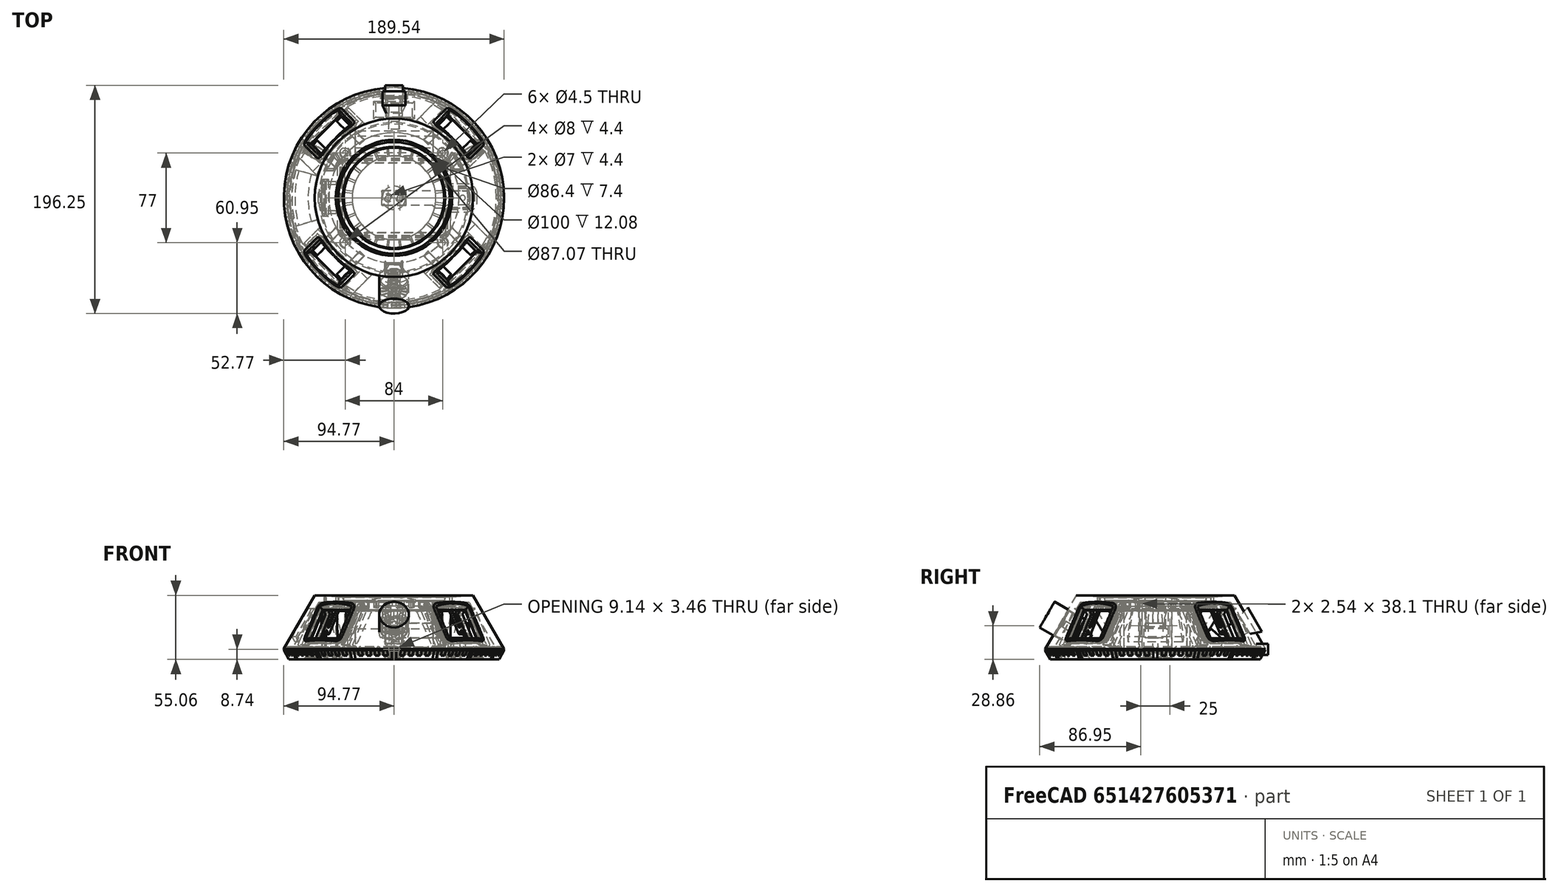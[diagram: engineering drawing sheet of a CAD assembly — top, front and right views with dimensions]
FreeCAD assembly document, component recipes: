
FREECAD ASSEMBLY — COMPONENT RECIPES ("case_v3_r2")

This assembly document has 20 components, labeled P0..P19 below (a component is one placed body or linked part). 20 of them carry a construction recipe — the FreeCAD feature program that regenerates the part from scratch, quoted from this document or its linked companion documents; the rest are supplied as boundary geometry only. No exploded tour is included for this assembly.
NOTE — document 2 of 2 of this assembly tour. The two overview renders and the header above are repeated from document 1; the component sections below continue where the previous document stopped.
COMPONENT P12 — recipe-attached ("link_loadcell", a linked part whose construction recipe lives in a companion FreeCAD document of the same project; that document's serialized recipe follows).
Construction recipe (the companion document, serialized — sketch geometry with constraints, then the solid features built on it; lengths are millimeters unless a unit is written):

FCSTD DOCUMENT  (FreeCAD 0.22R38340 (Git))
Label: parts_v3
License: All rights reserved
LicenseURL: https://en.wikipedia.org/wiki/All_rights_reserved
objects: PartDesign::Pad×24, Sketcher::SketchObject×20, Image::ImagePlane×7, PartDesign::Body×7, PartDesign::SubShapeBinder×2, PartDesign::Pocket×1
note: 124 computed .brp shape members not serialized (recipe doc carries the construction recipe); baked Part::Feature solids carry a one-line shape summary decoded from their .brp

FEATURE [Sketcher::SketchObject] Sketch001
  ArcFitTolerance = 1e-06
  AttachmentSupport = -> [XY_Plane001]
  FullyConstrained = false
  MakeInternals = false
  MapMode = 5
  sketch-geometry (26):
    g0: LineSegment StartX=-17.075 StartY=25.15 StartZ=0 EndX=-17.075 EndY=-31.25 EndZ=0
    g1: LineSegment StartX=-17.075 StartY=-31.25 StartZ=0 EndX=17.075 EndY=-31.25 EndZ=0
    g2: LineSegment StartX=17.075 StartY=-31.25 StartZ=0 EndX=17.075 EndY=25.149 EndZ=0
    g3: GeomPoint X=0 Y=0 Z=0
    g4: Circle CenterX=-15.125 CenterY=22.95 CenterZ=0 NormalX=0 NormalY=0 NormalZ=1 AngleXU=0 Radius=1
    g5: Circle CenterX=14.875 CenterY=22.95 CenterZ=0 NormalX=0 NormalY=0 NormalZ=1 AngleXU=0 Radius=1
    g6: Circle CenterX=14.875 CenterY=-29.05 CenterZ=0 NormalX=0 NormalY=0 NormalZ=1 AngleXU=0 Radius=1
    g7: Circle CenterX=-15.125 CenterY=-29.05 CenterZ=0 NormalX=0 NormalY=0 NormalZ=1 AngleXU=0 Radius=1
    g8: LineSegment StartX=-14.015 StartY=17.52 StartZ=0 EndX=-14.015 EndY=-17.52 EndZ=0
    g9: LineSegment StartX=-14.015 StartY=-17.52 StartZ=0 EndX=14.015 EndY=-17.52 EndZ=0
    g10: LineSegment StartX=14.015 StartY=-17.52 StartZ=0 EndX=14.015 EndY=17.52 EndZ=0
    g11: LineSegment StartX=14.015 StartY=17.52 StartZ=0 EndX=-14.015 EndY=17.52 EndZ=0
    g12: GeomPoint X=0 Y=0 Z=0
    g13: LineSegment StartX=-17.075 StartY=19.95 StartZ=0 EndX=-17.075 EndY=-23.9 EndZ=0
    g14: LineSegment StartX=-17.075 StartY=-23.9 StartZ=0 EndX=17.075 EndY=-23.9 EndZ=0
    g15: LineSegment StartX=17.075 StartY=-23.9 StartZ=0 EndX=17.075 EndY=19.95 EndZ=0
    g16: LineSegment StartX=17.075 StartY=19.95 StartZ=0 EndX=-17.075 EndY=19.95 EndZ=0
    g17: GeomPoint X=0 Y=-1.975 Z=0
    g18: LineSegment StartX=-11.575 StartY=25.149 StartZ=0 EndX=-11.575 EndY=20.95 EndZ=0
    g19: LineSegment StartX=-11.575 StartY=20.95 StartZ=0 EndX=11.575 EndY=20.95 EndZ=0
    g20: LineSegment StartX=11.575 StartY=20.95 StartZ=0 EndX=11.575 EndY=25.149 EndZ=0
    g21: LineSegment StartX=11.575 StartY=25.149 StartZ=0 EndX=-11.575 EndY=25.149 EndZ=0
    g22: LineSegment StartX=14.875 StartY=-29.05 StartZ=0 EndX=17.075 EndY=-29.05 EndZ=0
    g23: LineSegment StartX=-11.575 StartY=25.149 StartZ=0 EndX=11.575 EndY=25.149 EndZ=0
    g24: LineSegment StartX=-17.075 StartY=25.15 StartZ=0 EndX=-11.575 EndY=25.149 EndZ=0
    g25: LineSegment StartX=11.575 StartY=25.149 StartZ=0 EndX=17.075 EndY=25.149 EndZ=0
  constraints (67):
    c: Coincident(g0,g1)
    c: Coincident(g1,g2)
    c: Vertical(g0)
    c: Vertical(g2)
    c: Coincident(g3,g-1)
    c: DistanceY(g0,g0) = 56.4
    c: Equal(g5,g4)
    c: Equal(g4,g6)
    c: Equal(g6,g7)
    c: Diameter(g5) = 2
    c: Horizontal(g4,g5)
    c: Vertical(g5,g6)
    c: Vertical(g7,g4)
    c: DistanceX(g7,g6) = 30
    c: Coincident(g8,g9)
    c: Coincident(g9,g10)
    c: Coincident(g10,g11)
    c: Coincident(g11,g8)
    c: Vertical(g8)
    c: Vertical(g10)
    c: Horizontal(g9)
    c: Horizontal(g11)
    c: Symmetric(g10,g8,g12)
    c: Coincident(g12,g3)
    c: DistanceY(g8,g8) = 35.04
    c: DistanceX(g9,g9) = 28.03
    c: Coincident(g13,g14)
    c: Coincident(g14,g15)
    c: Coincident(g15,g16)
    c: Coincident(g16,g13)
    c: Vertical(g13)
    c: Vertical(g15)
    c: Horizontal(g14)
    c: Horizontal(g16)
    c: Symmetric(g15,g13,g17)
    c: PointOnObject(g17,g-2)
    c: DistanceY(g13,g13) = 43.85
    c: DistanceY(g7,g4) = 52
    c: DistanceY(g4,g0) = 2.2
    c: DistanceY(g13,g0) = 5.2
    c: Coincident(g18,g19)
    c: Coincident(g19,g20)
    c: Coincident(g20,g21)
    c: Coincident(g21,g18)
    c: Vertical(g18)
    c: Vertical(g20)
    c: Horizontal(g19)
    c: Symmetric(g20,g18,g-2)
    c: DistanceX(g20,g2) = 5.5
    c: DistanceY(g18,g0) = 0.001
    c: DistanceY(g19,g15) = -1
    c: DistanceY(g8,g13) = 2.43
    c: DistanceX(g16,g16) = 34.15
    c: DistanceX(g0,g2) = 34.15
    c: DistanceY(g1,g14) = 7.35
    c: Horizontal(g1)
    c: Coincident(g22,g6)
    c: PointOnObject(g22,g2)
    c: Horizontal(g22)
    c: DistanceX(g22,g22) = 2.2
    c: PointOnObject(g14,g2)
    c: Horizontal(g6,g7)
    c: Coincident(g23,g18)
    c: Coincident(g23,g20)
    c: Coincident(g25,g20)
    c: Coincident(g25,g2)
    c: Horizontal(g25)
FEATURE [Image::ImagePlane] lcd_front
  Placement = pos=(-11.6,7.22,10) rot=(0,0,1;0rad)
  XSize = 60.46
  YSize = 79.2117
FEATURE [Image::ImagePlane] lcd_side
  Placement = pos=(0,3.4,-17.75) rot=(0,1,0;1.5708rad)
  XSize = 52.9027
  YSize = 78.7888
FEATURE [PartDesign::SubShapeBinder] Binder
  BindCopyOnChange = 0
  BindMode = 0
  ClaimChildren = false
  Context = -> Body001 [Binder.]
  Fuse = false
  MakeFace = true
  OffsetFill = false
  OffsetIntersection = false
  OffsetJoinType = 0
  OffsetOpenResult = false
  PartialLoad = false
  Placement = pos=(0,0,3.85) rot=(0,0,1;0rad)
  Refine = true
  Relative = true
  Support = -> [Sketch001[Edge16,Edge15,Edge18,Edge17]]
  _Version = 2
  expr: .Placement.Base.z = Pad004.Length + 0.2 mm
FEATURE [Image::ImagePlane] charger  label="charger_img"
  XSize = 201.411
  YSize = 256.437
FEATURE [Sketcher::SketchObject] Sketch002
  ArcFitTolerance = 1e-06
  AttachmentSupport = -> [XY_Plane002]
  FullyConstrained = true
  MakeInternals = false
  MapMode = 5
  sketch-geometry (10):
    g0: LineSegment StartX=-6 StartY=0 StartZ=0 EndX=-6 EndY=-1.6 EndZ=0
    g1: LineSegment StartX=-6 StartY=-16 StartZ=0 EndX=6 EndY=-16 EndZ=0
    g2: LineSegment StartX=6 StartY=-16 StartZ=0 EndX=6 EndY=-3.2 EndZ=0
    g3: LineSegment StartX=6 StartY=0 StartZ=0 EndX=-6 EndY=0 EndZ=0
    g4: GeomPoint X=-6 Y=-2.4 Z=0
    g5: GeomPoint X=6 Y=-2.4 Z=0
    g6: ArcOfCircle CenterX=-6 CenterY=-2.4 CenterZ=0 NormalX=0 NormalY=0 NormalZ=1 AngleXU=0 Radius=0.8 StartAngle=4.71239 EndAngle=7.85398
    g7: ArcOfCircle CenterX=6 CenterY=-2.4 CenterZ=0 NormalX=0 NormalY=0 NormalZ=1 AngleXU=0 Radius=0.8 StartAngle=1.5708 EndAngle=4.71239
    g8: LineSegment StartX=6 StartY=-1.6 StartZ=0 EndX=6 EndY=0 EndZ=0
    g9: LineSegment StartX=-6 StartY=-3.2 StartZ=0 EndX=-6 EndY=-16 EndZ=0
  constraints (29):
    c: Coincident(g9,g1)
    c: Coincident(g1,g2)
    c: Coincident(g8,g3)
    c: Coincident(g3,g0)
    c: Vertical(g0)
    c: Vertical(g2)
    c: Horizontal(g1)
    c: Horizontal(g3)
    c: Distance(g0,g8) = 12
    c: Distance(g1,g3) = 16
    c: Symmetric(g0,g8,g-1)
    c: PointOnObject(g4,g0)
    c: PointOnObject(g5,g2)
    c: Horizontal(g5,g4)
    c: DistanceY(g4,g0) = 2.4
    c: Coincident(g6,g4)
    c: PointOnObject(g6,g9)
    c: Coincident(g7,g5)
    c: PointOnObject(g7,g8)
    c: Equal(g6,g7)
    c: Radius(g6) = 0.8
    c: Coincident(g2,g7)
    c: PointOnObject(g8,g7)
    c: Coincident(g0,g6)
    c: PointOnObject(g9,g6)
    c: Vertical(g0,g6)
    c: Vertical(g7,g2)
    c: Vertical(g9)
    c: Vertical(g8)
FEATURE [Sketcher::SketchObject] Sketch003
  ArcFitTolerance = 1e-06
  AttachmentOffset = pos=(0,0,-1.3) rot=(0,0,1;0rad)
  AttachmentSupport = -> [XZ_Plane002]
  FullyConstrained = true
  MakeInternals = false
  MapMode = 5
  Placement = pos=(0,1.3,-3e-16) rot=(1,0,0;1.5708rad)
  expr: Constraints[22] = 6.69 mm + 0.2 mm
  expr: Constraints[23] = 4.4 mm + 0.1 mm
  expr: Constraints[7] = 8.94 mm + 0.2 mm
  expr: Constraints[8] = 3.26 mm + 0.2 mm
  sketch-geometry (10):
    g0: LineSegment StartX=-3.445 StartY=1.04 StartZ=0 EndX=3.445 EndY=1.04 EndZ=0
    g1: LineSegment StartX=4.57 StartY=2.165 StartZ=0 EndX=4.57 EndY=3.375 EndZ=0
    g2: LineSegment StartX=3.445 StartY=4.5 StartZ=0 EndX=-3.445 EndY=4.5 EndZ=0
    g3: LineSegment StartX=-4.57 StartY=3.375 StartZ=0 EndX=-4.57 EndY=2.165 EndZ=0
    g4: GeomPoint X=4.57 Y=4.5 Z=0
    g5: GeomPoint X=0 Y=2.77 Z=0
    g6: ArcOfCircle CenterX=3.445 CenterY=3.375 CenterZ=0 NormalX=0 NormalY=0 NormalZ=1 AngleXU=0 Radius=1.125 StartAngle=0 EndAngle=1.5708
    g7: ArcOfCircle CenterX=3.445 CenterY=2.165 CenterZ=0 NormalX=0 NormalY=0 NormalZ=1 AngleXU=0 Radius=1.125 StartAngle=4.71239 EndAngle=6.28319
    g8: ArcOfCircle CenterX=-3.445 CenterY=2.165 CenterZ=0 NormalX=0 NormalY=0 NormalZ=1 AngleXU=0 Radius=1.125 StartAngle=3.14159 EndAngle=4.71239
    g9: ArcOfCircle CenterX=-3.445 CenterY=3.375 CenterZ=0 NormalX=0 NormalY=0 NormalZ=1 AngleXU=0 Radius=1.125 StartAngle=1.5708 EndAngle=3.14159
  constraints (24):
    c: Horizontal(g0)
    c: Horizontal(g2)
    c: Vertical(g1)
    c: Vertical(g3)
    c: Symmetric(g2,g0,g5)
    c: PointOnObject(g4,g1)
    c: PointOnObject(g4,g2)
    c: Distance(g1,g3) = 9.14
    c: Distance(g0,g2) = 3.46
    c: PointOnObject(g5,g-2)
    c: Equal(g3,g1)
    c: Equal(g0,g2)
    c: Vertical(g0,g2)
    c: DistanceY(g1,g1) = 1.21
    c: Tangent(g6,g2) = -1.5708
    c: Tangent(g6,g1) = -1.5708
    c: Tangent(g7,g1) = -1.5708
    c: Tangent(g7,g0) = -1.5708
    c: Tangent(g8,g0) = -1.5708
    c: Tangent(g8,g3) = -1.5708
    c: Tangent(g9,g3) = -1.5708
    c: Tangent(g9,g2) = -1.5708
    c: DistanceX(g2,g2) = 6.89
    c: DistanceY(g2) = 4.5
FEATURE [PartDesign::Pad] Pad007
  Direction = (0,-1,2e-16)
  Length = 10
  Length2 = 10
  Placement = pos=(0,0,0) rot=(1,0,0;1.5708rad)
  Profile = -> Sketch003
  ReferenceAxis = -> Sketch003 [N_Axis]
  Refine = true
  Suppressed = false
  Type = 0
FEATURE [PartDesign::SubShapeBinder] Binder001
  BindCopyOnChange = 0
  BindMode = 0
  ClaimChildren = false
  Context = -> Body002 [Binder001.]
  Fuse = false
  MakeFace = true
  Offset = 3
  OffsetFill = false
  OffsetIntersection = false
  OffsetJoinType = 0
  OffsetOpenResult = false
  PartialLoad = false
  Refine = true
  Relative = true
  Support = -> [Sketch003]
  _Version = 2
FEATURE [PartDesign::Pad] Pad008
  BaseFeature = -> Pad007
  Direction = (0,-1,2e-16)
  Length = 10
  Length2 = 10
  Placement = pos=(0,0,0) rot=(1,0,0;1.5708rad)
  Profile = -> Binder001
  Refine = true
  Reversed = true
  Suppressed = false
  Type = 0
FEATURE [Sketcher::SketchObject] Sketch005
  ArcFitTolerance = 1e-06
  AttachmentSupport = -> [XY_Plane004]
  FullyConstrained = false
  MakeInternals = false
  MapMode = 5
  sketch-geometry (5):
    g0: Circle CenterX=0 CenterY=0 CenterZ=0 NormalX=0 NormalY=0 NormalZ=1 AngleXU=0 Radius=9.25
    g1: ArcOfCircle CenterX=0 CenterY=0 CenterZ=0 NormalX=0 NormalY=0 NormalZ=1 AngleXU=0 Radius=9.25 StartAngle=0.74724 EndAngle=5.53526
    g2: LineSegment StartX=6.7855 StartY=6.28645 StartZ=0 EndX=11.637 EndY=1.04978 EndZ=0
    g3: ArcOfCircle CenterX=10.5 CenterY=-0.00362076 CenterZ=0 NormalX=0 NormalY=0 NormalZ=1 AngleXU=0 Radius=1.55 StartAngle=5.53526 EndAngle=7.03042
    g4: LineSegment StartX=11.6363 StartY=-1.05781 StartZ=0 EndX=6.78116 EndY=-6.29114 EndZ=0
  constraints (10):
    c: Diameter(g0) = 18.5
    c: Coincident(g0,g-1)
    c: Coincident(g1,g0)
    c: PointOnObject(g1,g0)
    c: Tangent(g2,g3) = 1.5708
    c: Coincident(g4,g1)
    c: Tangent(g4,g0)
    c: Tangent(g3,g4) = 1.5708
    c: Tangent(g1,g2) = 1.5708
    c: Radius(g3) = 1.55
FEATURE [Sketcher::SketchObject] Sketch006
  ArcFitTolerance = 1e-06
  AttachmentSupport = -> [XY_Plane005]
  FullyConstrained = true
  MakeInternals = false
  MapMode = 5
  sketch-geometry (8):
    g0: LineSegment StartX=-8.8 StartY=0 StartZ=0 EndX=-12.0492 EndY=10 EndZ=0
    g1: LineSegment StartX=-12.0492 StartY=10 StartZ=0 EndX=12.0492 EndY=10 EndZ=0
    g2: LineSegment StartX=12.0492 StartY=10 StartZ=0 EndX=8.8 EndY=0 EndZ=0
    g3: LineSegment StartX=8.8 StartY=0 StartZ=0 EndX=6.8 EndY=0 EndZ=0
    g4: LineSegment StartX=6.8 StartY=0 StartZ=0 EndX=6.8 EndY=-17 EndZ=0
    g5: LineSegment StartX=6.8 StartY=-17 StartZ=0 EndX=-6.8 EndY=-17 EndZ=0
    g6: LineSegment StartX=-6.8 StartY=-17 StartZ=0 EndX=-6.8 EndY=0 EndZ=0
    g7: LineSegment StartX=-6.8 StartY=0 StartZ=0 EndX=-8.8 EndY=0 EndZ=0
  constraints (22):
    c: PointOnObject(g0,g-1)
    c: Coincident(g0,g1)
    c: Coincident(g1,g2)
    c: PointOnObject(g2,g-1)
    c: Coincident(g2,g3)
    c: PointOnObject(g3,g-1)
    c: Coincident(g3,g4)
    c: Vertical(g4)
    c: Horizontal(g5)
    c: Coincident(g6,g7)
    c: Coincident(g7,g0)
    c: Vertical(g6)
    c: Symmetric(g1,g0,g-2)
    c: Symmetric(g6,g3,g-2)
    c: Equal(g3,g7)
    c: DistanceX(g7,g7) = 2
    c: DistanceX(g6,g3) = 13.6
    c: Angle(g2,g3) = 1.88496
    c: DistanceY(g1) = 10
    c: DistanceY(g5) = -17
    c: Coincident(g4,g5)
    c: Coincident(g5,g6)
FEATURE [Image::ImagePlane] switch  label="switch001"
  Placement = pos=(4.15,-14.6,0) rot=(0,0,1;0rad)
  XSize = 46.4854
  YSize = 52.5152
FEATURE [Image::ImagePlane] switch001  label="switch002"
  Placement = pos=(0,-14.7,16.1) rot=(0,1,0;1.5708rad)
  XSize = 46.585
  YSize = 52.6277
FEATURE [Sketcher::SketchObject] Sketch007
  ArcFitTolerance = 1e-06
  AttachmentSupport = -> [YZ_Plane005]
  ExternalGeometry = -> [Sketch006]
  FullyConstrained = false
  MakeInternals = false
  MapMode = 5
  Placement = pos=(0,0,0) rot=(0.57735,0.57735,0.57735;2.0944rad)
  sketch-geometry (12):
    g0: LineSegment StartX=9.98307 StartY=9.79369 StartZ=0 EndX=9.98307 EndY=-9.79369 EndZ=0
    g1: LineSegment StartX=9.98307 StartY=-9.79369 StartZ=0 EndX=0 EndY=-6.55 EndZ=0
    g2: LineSegment StartX=0 StartY=-6.55 StartZ=0 EndX=0 EndY=-4.55 EndZ=0
    g3: LineSegment StartX=0 StartY=-4.55 StartZ=0 EndX=-17 EndY=-4.55 EndZ=0
    g4: LineSegment StartX=-17 StartY=-4.55 StartZ=0 EndX=-17 EndY=4.55 EndZ=0
    g5: LineSegment StartX=-17 StartY=4.55 StartZ=0 EndX=0 EndY=4.55 EndZ=0
    g6: LineSegment StartX=0 StartY=4.55 StartZ=0 EndX=0 EndY=6.55 EndZ=0
    g7: LineSegment StartX=0 StartY=6.55 StartZ=0 EndX=9.98307 EndY=9.79369 EndZ=0
    g8: LineSegment StartX=-35.1614 StartY=30.2524 StartZ=0 EndX=-35.1614 EndY=-33.0132 EndZ=0
    g9: LineSegment StartX=-35.1614 StartY=-33.0132 StartZ=0 EndX=30.785 EndY=-33.0132 EndZ=0
    g10: LineSegment StartX=30.785 StartY=-33.0132 StartZ=0 EndX=30.785 EndY=30.2524 EndZ=0
    g11: LineSegment StartX=30.785 StartY=30.2524 StartZ=0 EndX=-35.1614 EndY=30.2524 EndZ=0
  constraints (29):
    c: Coincident(g0,g1)
    c: PointOnObject(g1,g-2)
    c: Coincident(g1,g2)
    c: PointOnObject(g2,g-2)
    c: Coincident(g2,g3)
    c: Horizontal(g3)
    c: Coincident(g3,g4)
    c: Vertical(g4)
    c: Coincident(g4,g5)
    c: PointOnObject(g5,g-2)
    c: Horizontal(g5)
    c: Coincident(g5,g6)
    c: PointOnObject(g6,g-2)
    c: Coincident(g6,g7)
    c: Coincident(g0,g7)
    c: Equal(g6,g2)
    c: Symmetric(g0,g0,g-1)
    c: Equal(g7,g1)
    c: DistanceY(g2,g5) = 9.1
    c: DistanceY(g2,g2) = 2
    c: Angle(g1,g2) = 1.88496
    c: Coincident(g8,g9)
    c: Coincident(g9,g10)
    c: Coincident(g10,g11)
    c: Coincident(g11,g8)
    c: Vertical(g8)
    c: Vertical(g10)
    c: Horizontal(g9)
    c: Horizontal(g11)
FEATURE [PartDesign::Pad] Pad015
  Direction = (0,0,1)
  Length = 40
  Length2 = 10
  Midplane = true
  Profile = -> Sketch006
  ReferenceAxis = -> Sketch006 [N_Axis]
  Refine = true
  Suppressed = false
  Type = 0
FEATURE [PartDesign::Pocket] Pocket
  BaseFeature = -> Pad015
  Direction = (-1,0,0)
  Length = 5
  Length2 = 5
  Midplane = true
  Profile = -> Sketch007
  ReferenceAxis = -> Sketch007 [N_Axis]
  Refine = true
  Suppressed = false
  Type = 1
FEATURE [PartDesign::Body] Body005  label="switch"
  AllowCompound = false
  Group = -> [Sketch006,Sketch007,Pad015,Pocket]
  Origin = -> Origin005
  Tip = -> Pocket
FEATURE [PartDesign::Pad] Pad021
  BaseFeature = -> Pad008
  Direction = (0,0,1)
  Length = 4.5
  Length2 = 10
  Placement = pos=(0,0,0) rot=(1,0,0;1.5708rad)
  Profile = -> Sketch002
  ReferenceAxis = -> Sketch002 [N_Axis]
  Refine = true
  Suppressed = false
  Type = 0
FEATURE [Sketcher::SketchObject] Sketch008
  ArcFitTolerance = 1e-06
  AttachmentOffset = pos=(0,0,2) rot=(0,0,1;0rad)
  AttachmentSupport = -> [XY_Plane002]
  FullyConstrained = true
  MakeInternals = false
  MapMode = 5
  Placement = pos=(0,0,2) rot=(0,0,1;0rad)
  sketch-geometry (4):
    g0: LineSegment StartX=-7 StartY=0 StartZ=0 EndX=-7 EndY=-16 EndZ=0
    g1: LineSegment StartX=-7 StartY=-16 StartZ=0 EndX=7 EndY=-16 EndZ=0
    g2: LineSegment StartX=7 StartY=-16 StartZ=0 EndX=7 EndY=0 EndZ=0
    g3: LineSegment StartX=7 StartY=0 StartZ=0 EndX=-7 EndY=0 EndZ=0
  constraints (11):
    c: Coincident(g0,g1)
    c: Coincident(g1,g2)
    c: Coincident(g2,g3)
    c: Coincident(g3,g0)
    c: Vertical(g0)
    c: Vertical(g2)
    c: Horizontal(g3)
    c: PointOnObject(g0,g-1)
    c: Symmetric(g1,g0,g-2)
    c: DistanceY(g1) = -16
    c: DistanceX(g1,g1) = 14
FEATURE [PartDesign::Pad] Pad022
  BaseFeature = -> Pad021
  Direction = (0,0,1)
  Length = 3
  Length2 = 10
  Placement = pos=(0,0,0) rot=(1,0,0;1.5708rad)
  Profile = -> Sketch008
  ReferenceAxis = -> Sketch008 [N_Axis]
  Refine = true
  Suppressed = false
  Type = 0
FEATURE [PartDesign::Body] Body002  label="charger"
  AllowCompound = false
  Group = -> [Sketch002,Sketch003,Pad007,Binder001,Pad008,Pad021,Sketch008,Pad022]
  Origin = -> Origin002
  Tip = -> Pad022
FEATURE [Sketcher::SketchObject] Sketch010
  ArcFitTolerance = 1e-06
  AttachmentSupport = -> [XY_Plane006]
  FullyConstrained = true
  MakeInternals = false
  MapMode = 5
  sketch-geometry (13):
    g0: Circle CenterX=-32 CenterY=0 CenterZ=0 NormalX=0 NormalY=0 NormalZ=1 AngleXU=0 Radius=2
    g1: Circle CenterX=-22 CenterY=0 CenterZ=0 NormalX=0 NormalY=0 NormalZ=1 AngleXU=0 Radius=2
    g2: Circle CenterX=22 CenterY=0 CenterZ=0 NormalX=0 NormalY=0 NormalZ=1 AngleXU=0 Radius=2
    g3: Circle CenterX=32 CenterY=0 CenterZ=0 NormalX=0 NormalY=0 NormalZ=1 AngleXU=0 Radius=2
    g4: LineSegment StartX=-37.5 StartY=6.35 StartZ=0 EndX=-37.5 EndY=-6.35 EndZ=0
    g5: LineSegment StartX=-37.5 StartY=-6.35 StartZ=0 EndX=37.5 EndY=-6.35 EndZ=0
    g6: LineSegment StartX=37.5 StartY=-6.35 StartZ=0 EndX=37.5 EndY=6.35 EndZ=0
    g7: GeomPoint X=0 Y=0 Z=0
    g8: LineSegment StartX=6.5 StartY=6.35 StartZ=0 EndX=8.8 EndY=8.65 EndZ=0
    g9: LineSegment StartX=8.8 StartY=8.65 StartZ=0 EndX=37.5 EndY=8.65 EndZ=0
    g10: LineSegment StartX=37.5 StartY=8.65 StartZ=0 EndX=37.5 EndY=6.35 EndZ=0
    g11: LineSegment StartX=6.5 StartY=6.35 StartZ=0 EndX=-37.5 EndY=6.35 EndZ=0
    g12: LineSegment StartX=37.5 StartY=8.65 StartZ=0 EndX=37.5 EndY=6.35 EndZ=0
  constraints (35):
    c: PointOnObject(g0,g-1)
    c: PointOnObject(g1,g-1)
    c: PointOnObject(g3,g-1)
    c: Equal(g3,g2)
    c: Equal(g2,g1)
    c: Equal(g1,g0)
    c: Coincident(g4,g5)
    c: Coincident(g5,g6)
    c: Coincident(g11,g4)
    c: Vertical(g4)
    c: Vertical(g6)
    c: Horizontal(g5)
    c: Symmetric(g6,g4,g7)
    c: Coincident(g7,g-1)
    c: DistanceX(g11,g6) = 75
    c: DistanceY(g6,g6) = 12.7
    c: DistanceX(g0,g1) = 10
    c: DistanceX(g2,g3) = 10
    c: Diameter(g1) = 4
    c: DistanceX(g1,g2) = 44
    c: Symmetric(g1,g2,g-2)
    c: PointOnObject(g8,g11)
    c: Coincident(g8,g9)
    c: Horizontal(g9)
    c: Coincident(g10,g6)
    c: Vertical(g10)
    c: PointOnObject(g11,g8)
    c: Coincident(g9,g10)
    c: DistanceY(g5,g8) = 15
    c: Angle(g8,g9) = 2.35619
    c: DistanceX(g8,g6) = 31
    c: Horizontal(g11)
    c: Horizontal(g8,g6)
    c: Coincident(g12,g9)
    c: Coincident(g12,g6)
FEATURE [PartDesign::Pad] Pad024
  Direction = (0,0,1)
  Length = 12.7
  Length2 = 10
  Profile = -> Sketch010 [Edge7,Edge6,Edge5,Edge11,Edge10,Edge9,Edge8]
  ReferenceAxis = -> Sketch010 [N_Axis]
  Refine = true
  Suppressed = false
  Type = 0
FEATURE [PartDesign::Pad] Pad025  label="Pad_LOAD_SCREWS"
  BaseFeature = -> Pad024
  Direction = (0,0,1)
  Length = 15
  Length2 = 10
  Profile = -> Sketch010 [Edge1,Edge2]
  ReferenceAxis = -> Sketch010 [N_Axis]
  Refine = true
  Reversed = true
  Suppressed = false
  Type = 0
FEATURE [PartDesign::Pad] Pad026  label="Pad_FIXED_SCREWS"
  BaseFeature = -> Pad025
  Direction = (0,0,1)
  Length = 25
  Length2 = 10
  Profile = -> Sketch010 [Edge3,Edge4]
  ReferenceAxis = -> Sketch010 [N_Axis]
  Refine = true
  Suppressed = false
  Type = 0
FEATURE [PartDesign::Body] Body006  label="loadcell_mit_silikon"
  AllowCompound = false
  Group = -> [Sketch010,Pad024,Pad025,Pad026]
  Origin = -> Origin006
  Tip = -> Pad026
FEATURE [Sketcher::SketchObject] Sketch011
  ArcFitTolerance = 1e-06
  AttachmentSupport = -> [XY_Plane001]
  FullyConstrained = false
  MakeInternals = false
  MapMode = 5
  sketch-geometry (4):
    g0: LineSegment StartX=-19.075 StartY=27.15 StartZ=0 EndX=-19.075 EndY=-33.25 EndZ=0
    g1: LineSegment StartX=-19.075 StartY=-33.25 StartZ=0 EndX=17.075 EndY=-33.25 EndZ=0
    g2: LineSegment StartX=17.075 StartY=-33.25 StartZ=0 EndX=17.075 EndY=27.15 EndZ=0
    g3: LineSegment StartX=17.075 StartY=27.15 StartZ=0 EndX=-19.075 EndY=27.15 EndZ=0
  constraints (8):
    c: Coincident(g0,g1)
    c: Coincident(g1,g2)
    c: Coincident(g2,g3)
    c: Coincident(g3,g0)
    c: Vertical(g0)
    c: Vertical(g2)
    c: Horizontal(g1)
    c: Horizontal(g3)
FEATURE [PartDesign::Pad] Pad027
  Direction = (0,0,1)
  Length = 1.2
  Length2 = 10
  Profile = -> Sketch011
  ReferenceAxis = -> Sketch011 [N_Axis]
  Refine = true
  Suppressed = false
  Type = 0
FEATURE [PartDesign::Pad] Pad004
  BaseFeature = -> Pad027
  Direction = (0,0,1)
  Length = 3.65
  Length2 = 10
  Profile = -> Sketch001 [Edge21,Edge20,Edge19,Edge22]
  ReferenceAxis = -> Sketch001 [N_Axis]
  Refine = true
  Suppressed = false
  Type = 0
FEATURE [PartDesign::Pad] Pad005
  BaseFeature = -> Pad004
  Direction = (0,0,1)
  Length = 10
  Length2 = 1
  Profile = -> Binder
  Refine = true
  Suppressed = false
  TaperAngle = 35
  Type = 4
FEATURE [PartDesign::Pad] Pad028
  BaseFeature = -> Pad005
  Direction = (0,0,1)
  Length = 3.5
  Length2 = 10
  Profile = -> Sketch001 [Edge1,Edge4,Edge3,Edge2]
  ReferenceAxis = -> Sketch001 [N_Axis]
  Refine = true
  Suppressed = false
  TaperAngle = -10
  Type = 4
FEATURE [PartDesign::Body] Body001  label="display"
  AllowCompound = false
  Group = -> [Sketch001,Sketch011,Pad027,Pad004,Binder,Pad005,Pad028]
  Origin = -> Origin001
  Tip = -> Pad028
FEATURE [Sketcher::SketchObject] Sketch012
  ArcFitTolerance = 1e-06
  AttachmentSupport = -> [XY_Plane007]
  FullyConstrained = true
  MakeInternals = false
  MapMode = 5
  sketch-geometry (4):
    g0: LineSegment StartX=-5.9 StartY=7.25 StartZ=0 EndX=-5.9 EndY=-7.25 EndZ=0
    g1: LineSegment StartX=-5.9 StartY=-7.25 StartZ=0 EndX=5.9 EndY=-7.25 EndZ=0
    g2: LineSegment StartX=5.9 StartY=-7.25 StartZ=0 EndX=5.9 EndY=7.25 EndZ=0
    g3: LineSegment StartX=5.9 StartY=7.25 StartZ=0 EndX=-5.9 EndY=7.25 EndZ=0
  constraints (11):
    c: Coincident(g0,g1)
    c: Coincident(g1,g2)
    c: Coincident(g2,g3)
    c: Coincident(g3,g0)
    c: Vertical(g0)
    c: Vertical(g2)
    c: Horizontal(g1)
    c: Horizontal(g3)
    c: DistanceX(g3,g3) = 11.8
    c: Symmetric(g0,g2,g-1)
    c: DistanceY(g2,g2) = 14.5
FEATURE [PartDesign::Pad] Pad009
  Direction = (0,0,1)
  Length = 6.5
  Length2 = 10
  Profile = -> Sketch012
  ReferenceAxis = -> Sketch012 [N_Axis]
  Refine = true
  Reversed = true
  Suppressed = false
  Type = 0
FEATURE [Sketcher::SketchObject] Sketch013
  ArcFitTolerance = 1e-06
  AttachmentSupport = -> [XY_Plane007]
  FullyConstrained = true
  MakeInternals = false
  MapMode = 5
  sketch-geometry (1):
    g0: Circle CenterX=0 CenterY=0 CenterZ=0 NormalX=0 NormalY=0 NormalZ=1 AngleXU=0 Radius=3.5
  constraints (2):
    c: Diameter(g0) = 7
    c: Coincident(g0,g-1)
FEATURE [PartDesign::Pad] Pad010
  BaseFeature = -> Pad009
  Direction = (0,0,1)
  Length = 5
  Length2 = 10
  Profile = -> Sketch013
  ReferenceAxis = -> Sketch013 [N_Axis]
  Refine = true
  Suppressed = false
  Type = 0
FEATURE [Sketcher::SketchObject] Sketch014
  ArcFitTolerance = 1e-06
  AttachmentSupport = -> [XY_Plane007]
  FullyConstrained = true
  MakeInternals = false
  MapMode = 5
  sketch-geometry (1):
    g0: Circle CenterX=0 CenterY=0 CenterZ=0 NormalX=0 NormalY=0 NormalZ=1 AngleXU=0 Radius=3
  constraints (2):
    c: Diameter(g0) = 6
    c: Coincident(g0,g-1)
FEATURE [PartDesign::Pad] Pad011
  BaseFeature = -> Pad010
  Direction = (0,0,1)
  Length = 15
  Length2 = 10
  Profile = -> Sketch014
  ReferenceAxis = -> Sketch014 [N_Axis]
  Refine = true
  Suppressed = false
  Type = 0
FEATURE [Sketcher::SketchObject] Sketch015
  ArcFitTolerance = 1e-06
  AttachmentSupport = -> [XY_Plane007]
  FullyConstrained = false
  MakeInternals = false
  MapMode = 5
  sketch-geometry (8):
    g0: LineSegment StartX=-4.4052 StartY=7.5 StartZ=0 EndX=-4.4052 EndY=6.5 EndZ=0
    g1: LineSegment StartX=-4.4052 StartY=6.5 StartZ=0 EndX=4.47502 EndY=6.5 EndZ=0
    g2: LineSegment StartX=4.47502 StartY=6.5 StartZ=0 EndX=4.47502 EndY=7.5 EndZ=0
    g3: LineSegment StartX=4.47502 StartY=7.5 StartZ=0 EndX=-4.4052 EndY=7.5 EndZ=0
    g4: LineSegment StartX=-4.24166 StartY=-7 StartZ=0 EndX=-4.24166 EndY=-8 EndZ=0
    g5: LineSegment StartX=-4.24166 StartY=-8 StartZ=0 EndX=5.13629 EndY=-8 EndZ=0
    g6: LineSegment StartX=5.13629 StartY=-8 StartZ=0 EndX=5.13629 EndY=-7 EndZ=0
    g7: LineSegment StartX=5.13629 StartY=-7 StartZ=0 EndX=-4.24166 EndY=-7 EndZ=0
  constraints (20):
    c: Coincident(g0,g1)
    c: Coincident(g1,g2)
    c: Coincident(g2,g3)
    c: Coincident(g3,g0)
    c: Vertical(g0)
    c: Vertical(g2)
    c: Horizontal(g1)
    c: Horizontal(g3)
    c: Coincident(g4,g5)
    c: Coincident(g5,g6)
    c: Coincident(g6,g7)
    c: Coincident(g7,g4)
    c: Vertical(g4)
    c: Vertical(g6)
    c: Horizontal(g5)
    c: Horizontal(g7)
    c: DistanceY(g4) = -7
    c: DistanceY(g4,g4) = 1
    c: DistanceY(g0) = 6.5
    c: DistanceY(g0,g0) = 1
FEATURE [PartDesign::Pad] Pad012
  BaseFeature = -> Pad011
  Direction = (0,0,1)
  Length = 10
  Length2 = 10
  Profile = -> Sketch015
  ReferenceAxis = -> Sketch015 [N_Axis]
  Refine = true
  Reversed = true
  Suppressed = false
  Type = 0
FEATURE [PartDesign::Body] Body007  label="Encoder"
  AllowCompound = false
  Group = -> [Sketch012,Pad009,Sketch013,Pad010,Sketch014,Pad011,Sketch015,Pad012]
  Origin = -> Origin007
  Tip = -> Pad012
FEATURE [Sketcher::SketchObject] Sketch016
  ArcFitTolerance = 1e-06
  AttachmentSupport = -> [XY_Plane008]
  FullyConstrained = false
  MakeInternals = false
  MapMode = 5
  sketch-geometry (5):
    g0: LineSegment StartX=0 StartY=14.25 StartZ=0 EndX=0 EndY=-14.25 EndZ=0
    g1: LineSegment StartX=0 StartY=-14.25 StartZ=0 EndX=52 EndY=-14.25 EndZ=0
    g2: LineSegment StartX=52 StartY=-14.25 StartZ=0 EndX=52 EndY=14.25 EndZ=0
    g3: LineSegment StartX=52 StartY=14.25 StartZ=0 EndX=0 EndY=14.25 EndZ=0
    g4: GeomPoint X=49.5 Y=0 Z=0
  constraints (12):
    c: Coincident(g0,g1)
    c: Coincident(g1,g2)
    c: Coincident(g2,g3)
    c: Coincident(g3,g0)
    c: Vertical(g2)
    c: Horizontal(g1)
    c: Horizontal(g3)
    c: DistanceX(g1,g1) = 52
    c: DistanceY(g2,g2) = 28.5
    c: PointOnObject(g4,g-1)
    c: PointOnObject(g0,g-2)
    c: Symmetric(g0,g0,g-1)
FEATURE [PartDesign::Pad] Pad001
  Direction = (0,0,1)
  Length = 1.2
  Length2 = 10
  Profile = -> Sketch016 [Edge4,Edge1,Edge2,Edge3]
  ReferenceAxis = -> Sketch016 [N_Axis]
  Refine = true
  Suppressed = false
  Type = 0
FEATURE [Sketcher::SketchObject] Sketch017
  ArcFitTolerance = 1e-06
  AttachmentSupport = -> [XY_Plane008]
  FullyConstrained = true
  MakeInternals = false
  MapMode = 5
  sketch-geometry (4):
    g0: LineSegment StartX=0 StartY=9 StartZ=0 EndX=0 EndY=-9 EndZ=0
    g1: LineSegment StartX=0 StartY=-9 StartZ=0 EndX=26 EndY=-9 EndZ=0
    g2: LineSegment StartX=26 StartY=-9 StartZ=0 EndX=26 EndY=9 EndZ=0
    g3: LineSegment StartX=26 StartY=9 StartZ=0 EndX=0 EndY=9 EndZ=0
  constraints (11):
    c: Coincident(g0,g1)
    c: Coincident(g1,g2)
    c: Coincident(g2,g3)
    c: Coincident(g3,g0)
    c: Parallel(g0,g2)
    c: Parallel(g1,g3)
    c: Perpendicular(g0,g1)
    c: PointOnObject(g0,g-2)
    c: DistanceX(g1,g1) = 26
    c: DistanceY(g2,g2) = 18
    c: Symmetric(g0,g0,g-1)
FEATURE [PartDesign::Pad] Pad003
  BaseFeature = -> Pad001
  Direction = (0,0,1)
  Length = 2
  Length2 = 10
  Profile = -> Sketch017
  ReferenceAxis = -> Sketch017 [N_Axis]
  Refine = true
  Suppressed = false
  Type = 0
FEATURE [Sketcher::SketchObject] Sketch018
  ArcFitTolerance = 1e-06
  AttachmentSupport = -> [XY_Plane008]
  FullyConstrained = true
  MakeInternals = false
  MapMode = 5
  sketch-geometry (5):
    g0: LineSegment StartX=7 StartY=-8 StartZ=0 EndX=25 EndY=-8 EndZ=0
    g1: LineSegment StartX=25 StartY=-8 StartZ=0 EndX=25 EndY=8 EndZ=0
    g2: LineSegment StartX=25 StartY=8 StartZ=0 EndX=7 EndY=8 EndZ=0
    g3: LineSegment StartX=7 StartY=8 StartZ=0 EndX=7 EndY=-8 EndZ=0
    g4: GeomPoint X=16 Y=3e-16 Z=0
  constraints (12):
    c: Coincident(g0,g1)
    c: Coincident(g1,g2)
    c: Coincident(g2,g3)
    c: Coincident(g3,g0)
    c: Horizontal(g0)
    c: Horizontal(g2)
    c: Vertical(g1)
    c: Symmetric(g2,g0,g4)
    c: Distance(g1,g3) = 18
    c: Distance(g0,g2) = 16
    c: Symmetric(g0,g2,g-1)
    c: DistanceX(g0) = 7
FEATURE [PartDesign::Pad] Pad029
  BaseFeature = -> Pad003
  Direction = (0,0,1)
  Length = 4.3
  Length2 = 10
  Profile = -> Sketch018
  ReferenceAxis = -> Sketch018 [N_Axis]
  Refine = true
  Suppressed = false
  Type = 0
FEATURE [Sketcher::SketchObject] Sketch004
  ArcFitTolerance = 1e-06
  AttachmentOffset = pos=(0,0,46) rot=(0,0,1;0rad)
  AttachmentSupport = -> [YZ_Plane008]
  FullyConstrained = true
  MakeInternals = false
  MapMode = 5
  Placement = pos=(46,0,0) rot=(0.57735,0.57735,0.57735;2.0944rad)
  sketch-geometry (9):
    g0: LineSegment StartX=-3.445 StartY=1.2 StartZ=0 EndX=3.445 EndY=1.2 EndZ=0
    g1: LineSegment StartX=4.57 StartY=2.325 StartZ=0 EndX=4.57 EndY=3.535 EndZ=0
    g2: LineSegment StartX=3.445 StartY=4.66 StartZ=0 EndX=-3.445 EndY=4.66 EndZ=0
    g3: LineSegment StartX=-4.57 StartY=3.535 StartZ=0 EndX=-4.57 EndY=2.325 EndZ=0
    g4: GeomPoint X=0 Y=2.93 Z=0
    g5: ArcOfCircle CenterX=3.445 CenterY=3.535 CenterZ=0 NormalX=0 NormalY=0 NormalZ=1 AngleXU=0 Radius=1.125 StartAngle=0 EndAngle=1.5708
    g6: ArcOfCircle CenterX=3.445 CenterY=2.325 CenterZ=0 NormalX=0 NormalY=0 NormalZ=1 AngleXU=0 Radius=1.125 StartAngle=4.71239 EndAngle=6.28319
    g7: ArcOfCircle CenterX=-3.445 CenterY=2.325 CenterZ=0 NormalX=0 NormalY=0 NormalZ=1 AngleXU=0 Radius=1.125 StartAngle=3.14159 EndAngle=4.71239
    g8: ArcOfCircle CenterX=-3.445 CenterY=3.535 CenterZ=0 NormalX=0 NormalY=0 NormalZ=1 AngleXU=0 Radius=1.125 StartAngle=1.5708 EndAngle=3.14159
  constraints (21):
    c: Horizontal(g0)
    c: Horizontal(g2)
    c: Vertical(g1)
    c: Vertical(g3)
    c: Symmetric(g2,g0,g4)
    c: Distance(g1,g3) = 9.14
    c: Distance(g0,g2) = 3.46
    c: PointOnObject(g4,g-2)
    c: Equal(g3,g1)
    c: Equal(g0,g2)
    c: Vertical(g0,g2)
    c: DistanceY(g1,g1) = 1.21
    c: Tangent(g5,g2) = -1.5708
    c: Tangent(g5,g1) = -1.5708
    c: Tangent(g6,g1) = -1.5708
    c: Tangent(g6,g0) = -1.5708
    c: Tangent(g7,g0) = -1.5708
    c: Tangent(g7,g3) = -1.5708
    c: Tangent(g8,g3) = -1.5708
    c: Tangent(g8,g2) = -1.5708
    c: DistanceY(g0) = 1.2
FEATURE [PartDesign::Pad] Pad030
  BaseFeature = -> Pad029
  Direction = (1,0,0)
  Length = 7.3
  Length2 = 10
  Profile = -> Sketch004
  ReferenceAxis = -> Sketch004 [N_Axis]
  Refine = true
  Suppressed = false
  Type = 0
FEATURE [Sketcher::SketchObject] Sketch019
  ArcFitTolerance = 1e-06
  AttachmentSupport = -> [XY_Plane008]
  FullyConstrained = true
  MakeInternals = false
  MapMode = 5
  sketch-geometry (5):
    g0: LineSegment StartX=27 StartY=-10 StartZ=0 EndX=51 EndY=-10 EndZ=0
    g1: LineSegment StartX=51 StartY=-10 StartZ=0 EndX=51 EndY=10 EndZ=0
    g2: LineSegment StartX=51 StartY=10 StartZ=0 EndX=27 EndY=10 EndZ=0
    g3: LineSegment StartX=27 StartY=10 StartZ=0 EndX=27 EndY=-10 EndZ=0
    g4: GeomPoint X=39 Y=-2e-16 Z=0
  constraints (13):
    c: Coincident(g0,g1)
    c: Coincident(g1,g2)
    c: Coincident(g2,g3)
    c: Coincident(g3,g0)
    c: Horizontal(g0)
    c: Horizontal(g2)
    c: Vertical(g1)
    c: Vertical(g3)
    c: Symmetric(g2,g0,g4)
    c: PointOnObject(g4,g-1)
    c: DistanceX(g0) = 27
    c: DistanceX(g0,g0) = 24
    c: DistanceY(g1,g1) = 20
FEATURE [PartDesign::Pad] Pad006
  BaseFeature = -> Pad030
  Direction = (0,0,1)
  Length = 3.5
  Length2 = 10
  Profile = -> Sketch019
  ReferenceAxis = -> Sketch019 [N_Axis]
  Refine = true
  Suppressed = false
  Type = 0
FEATURE [Sketcher::SketchObject] Sketch020
  ArcFitTolerance = 1e-06
  AttachmentSupport = -> [XY_Plane008]
  FullyConstrained = true
  MakeInternals = false
  MapMode = 5
  sketch-geometry (10):
    g0: LineSegment StartX=5.4 StartY=13.77 StartZ=0 EndX=5.4 EndY=11.23 EndZ=0
    g1: LineSegment StartX=5.4 StartY=11.23 StartZ=0 EndX=43.5 EndY=11.23 EndZ=0
    g2: LineSegment StartX=43.5 StartY=11.23 StartZ=0 EndX=43.5 EndY=13.77 EndZ=0
    g3: LineSegment StartX=43.5 StartY=13.77 StartZ=0 EndX=5.4 EndY=13.77 EndZ=0
    g4: GeomPoint X=24.45 Y=12.5 Z=0
    g5: LineSegment StartX=5.4 StartY=-13.77 StartZ=0 EndX=5.4 EndY=-11.23 EndZ=0
    g6: LineSegment StartX=5.4 StartY=-11.23 StartZ=0 EndX=43.5 EndY=-11.23 EndZ=0
    g7: LineSegment StartX=43.5 StartY=-11.23 StartZ=0 EndX=43.5 EndY=-13.77 EndZ=0
    g8: LineSegment StartX=43.5 StartY=-13.77 StartZ=0 EndX=5.4 EndY=-13.77 EndZ=0
    g9: GeomPoint X=24.45 Y=-12.5 Z=0
  constraints (25):
    c: Coincident(g0,g1)
    c: Coincident(g1,g2)
    c: Coincident(g2,g3)
    c: Coincident(g3,g0)
    c: Vertical(g0)
    c: Vertical(g2)
    c: Horizontal(g1)
    c: Horizontal(g3)
    c: Symmetric(g2,g0,g4)
    c: DistanceX(g1,g1) = 38.1
    c: DistanceX(g0) = 5.4
    c: DistanceY(g2,g2) = 2.54
    c: Coincident(g5,g6)
    c: Coincident(g6,g7)
    c: Coincident(g7,g8)
    c: Coincident(g8,g5)
    c: Vertical(g5)
    c: Vertical(g7)
    c: Horizontal(g6)
    c: Horizontal(g8)
    c: Symmetric(g7,g5,g9)
    c: DistanceY(g5,g0) = 25
    c: Equal(g5,g0)
    c: Equal(g6,g1)
    c: Symmetric(g5,g0,g-1)
FEATURE [PartDesign::Pad] Pad031
  BaseFeature = -> Pad006
  Direction = (0,0,1)
  Length = 8.5
  Length2 = 3.5
  Profile = -> Sketch020
  ReferenceAxis = -> Sketch020 [N_Axis]
  Refine = true
  Reversed = true
  Suppressed = false
  Type = 4
FEATURE [Sketcher::SketchObject] Sketch021
  ArcFitTolerance = 1e-06
  AttachmentSupport = -> [XY_Plane008]
  FullyConstrained = false
  MakeInternals = false
  MapMode = 5
  sketch-geometry (120):
    g0: LineSegment StartX=6.5 StartY=12.82 StartZ=0 EndX=6.5 EndY=12.18 EndZ=0
    g1: LineSegment StartX=6.5 StartY=12.18 StartZ=0 EndX=7.14 EndY=12.18 EndZ=0
    g2: LineSegment StartX=7.14 StartY=12.18 StartZ=0 EndX=7.14 EndY=12.82 EndZ=0
    g3: LineSegment StartX=7.14 StartY=12.82 StartZ=0 EndX=6.5 EndY=12.82 EndZ=0
    g4: LineSegment StartX=6.5 StartY=-12.18 StartZ=0 EndX=6.5 EndY=-12.82 EndZ=0
    g5: LineSegment StartX=6.5 StartY=-12.82 StartZ=0 EndX=7.14 EndY=-12.82 EndZ=0
    g6: LineSegment StartX=7.14 StartY=-12.82 StartZ=0 EndX=7.14 EndY=-12.18 EndZ=0
    g7: LineSegment StartX=7.14 StartY=-12.18 StartZ=0 EndX=6.5 EndY=-12.18 EndZ=0
    g8: LineSegment StartX=9.04 StartY=12.82 StartZ=0 EndX=9.04 EndY=12.18 EndZ=0
    g9: LineSegment StartX=9.04 StartY=12.18 StartZ=0 EndX=9.68 EndY=12.18 EndZ=0
    g10: LineSegment StartX=9.68 StartY=12.18 StartZ=0 EndX=9.68 EndY=12.82 EndZ=0
    g11: LineSegment StartX=9.68 StartY=12.82 StartZ=0 EndX=9.04 EndY=12.82 EndZ=0
    g12: LineSegment StartX=9.04 StartY=-12.18 StartZ=0 EndX=9.04 EndY=-12.82 EndZ=0
    g13: LineSegment StartX=9.04 StartY=-12.82 StartZ=0 EndX=9.68 EndY=-12.82 EndZ=0
    g14: LineSegment StartX=9.68 StartY=-12.82 StartZ=0 EndX=9.68 EndY=-12.18 EndZ=0
    g15: LineSegment StartX=9.68 StartY=-12.18 StartZ=0 EndX=9.04 EndY=-12.18 EndZ=0
    g16: LineSegment StartX=11.58 StartY=12.82 StartZ=0 EndX=11.58 EndY=12.18 EndZ=0
    g17: LineSegment StartX=11.58 StartY=12.18 StartZ=0 EndX=12.22 EndY=12.18 EndZ=0
    g18: LineSegment StartX=12.22 StartY=12.18 StartZ=0 EndX=12.22 EndY=12.82 EndZ=0
    g19: LineSegment StartX=12.22 StartY=12.82 StartZ=0 EndX=11.58 EndY=12.82 EndZ=0
    g20: LineSegment StartX=11.58 StartY=-12.18 StartZ=0 EndX=11.58 EndY=-12.82 EndZ=0
    g21: LineSegment StartX=11.58 StartY=-12.82 StartZ=0 EndX=12.22 EndY=-12.82 EndZ=0
    g22: LineSegment StartX=12.22 StartY=-12.82 StartZ=0 EndX=12.22 EndY=-12.18 EndZ=0
    g23: LineSegment StartX=12.22 StartY=-12.18 StartZ=0 EndX=11.58 EndY=-12.18 EndZ=0
    g24: LineSegment StartX=14.12 StartY=12.82 StartZ=0 EndX=14.12 EndY=12.18 EndZ=0
    g25: LineSegment StartX=14.12 StartY=12.18 StartZ=0 EndX=14.76 EndY=12.18 EndZ=0
    g26: LineSegment StartX=14.76 StartY=12.18 StartZ=0 EndX=14.76 EndY=12.82 EndZ=0
    g27: LineSegment StartX=14.76 StartY=12.82 StartZ=0 EndX=14.12 EndY=12.82 EndZ=0
    g28: LineSegment StartX=14.12 StartY=-12.18 StartZ=0 EndX=14.12 EndY=-12.82 EndZ=0
    g29: LineSegment StartX=14.12 StartY=-12.82 StartZ=0 EndX=14.76 EndY=-12.82 EndZ=0
    g30: LineSegment StartX=14.76 StartY=-12.82 StartZ=0 EndX=14.76 EndY=-12.18 EndZ=0
    g31: LineSegment StartX=14.76 StartY=-12.18 StartZ=0 EndX=14.12 EndY=-12.18 EndZ=0
    g32: LineSegment StartX=16.66 StartY=12.82 StartZ=0 EndX=16.66 EndY=12.18 EndZ=0
    g33: LineSegment StartX=16.66 StartY=12.18 StartZ=0 EndX=17.3 EndY=12.18 EndZ=0
    g34: LineSegment StartX=17.3 StartY=12.18 StartZ=0 EndX=17.3 EndY=12.82 EndZ=0
    g35: LineSegment StartX=17.3 StartY=12.82 StartZ=0 EndX=16.66 EndY=12.82 EndZ=0
    g36: LineSegment StartX=16.66 StartY=-12.18 StartZ=0 EndX=16.66 EndY=-12.82 EndZ=0
    g37: LineSegment StartX=16.66 StartY=-12.82 StartZ=0 EndX=17.3 EndY=-12.82 EndZ=0
    g38: LineSegment StartX=17.3 StartY=-12.82 StartZ=0 EndX=17.3 EndY=-12.18 EndZ=0
    g39: LineSegment StartX=17.3 StartY=-12.18 StartZ=0 EndX=16.66 EndY=-12.18 EndZ=0
    g40: LineSegment StartX=19.2 StartY=12.82 StartZ=0 EndX=19.2 EndY=12.18 EndZ=0
    g41: LineSegment StartX=19.2 StartY=12.18 StartZ=0 EndX=19.84 EndY=12.18 EndZ=0
    g42: LineSegment StartX=19.84 StartY=12.18 StartZ=0 EndX=19.84 EndY=12.82 EndZ=0
    g43: LineSegment StartX=19.84 StartY=12.82 StartZ=0 EndX=19.2 EndY=12.82 EndZ=0
    g44: LineSegment StartX=19.2 StartY=-12.18 StartZ=0 EndX=19.2 EndY=-12.82 EndZ=0
    g45: LineSegment StartX=19.2 StartY=-12.82 StartZ=0 EndX=19.84 EndY=-12.82 EndZ=0
    g46: LineSegment StartX=19.84 StartY=-12.82 StartZ=0 EndX=19.84 EndY=-12.18 EndZ=0
    g47: LineSegment StartX=19.84 StartY=-12.18 StartZ=0 EndX=19.2 EndY=-12.18 EndZ=0
    g48: LineSegment StartX=21.74 StartY=12.82 StartZ=0 EndX=21.74 EndY=12.18 EndZ=0
    g49: LineSegment StartX=21.74 StartY=12.18 StartZ=0 EndX=22.38 EndY=12.18 EndZ=0
    g50: LineSegment StartX=22.38 StartY=12.18 StartZ=0 EndX=22.38 EndY=12.82 EndZ=0
    g51: LineSegment StartX=22.38 StartY=12.82 StartZ=0 EndX=21.74 EndY=12.82 EndZ=0
    g52: LineSegment StartX=21.74 StartY=-12.18 StartZ=0 EndX=21.74 EndY=-12.82 EndZ=0
    g53: LineSegment StartX=21.74 StartY=-12.82 StartZ=0 EndX=22.38 EndY=-12.82 EndZ=0
    g54: LineSegment StartX=22.38 StartY=-12.82 StartZ=0 EndX=22.38 EndY=-12.18 EndZ=0
    g55: LineSegment StartX=22.38 StartY=-12.18 StartZ=0 EndX=21.74 EndY=-12.18 EndZ=0
    g56: LineSegment StartX=24.28 StartY=12.82 StartZ=0 EndX=24.28 EndY=12.18 EndZ=0
    g57: LineSegment StartX=24.28 StartY=12.18 StartZ=0 EndX=24.92 EndY=12.18 EndZ=0
    g58: LineSegment StartX=24.92 StartY=12.18 StartZ=0 EndX=24.92 EndY=12.82 EndZ=0
    g59: LineSegment StartX=24.92 StartY=12.82 StartZ=0 EndX=24.28 EndY=12.82 EndZ=0
    g60: LineSegment StartX=24.28 StartY=-12.18 StartZ=0 EndX=24.28 EndY=-12.82 EndZ=0
    g61: LineSegment StartX=24.28 StartY=-12.82 StartZ=0 EndX=24.92 EndY=-12.82 EndZ=0
    g62: LineSegment StartX=24.92 StartY=-12.82 StartZ=0 EndX=24.92 EndY=-12.18 EndZ=0
    g63: LineSegment StartX=24.92 StartY=-12.18 StartZ=0 EndX=24.28 EndY=-12.18 EndZ=0
    g64: LineSegment StartX=26.82 StartY=12.82 StartZ=0 EndX=26.82 EndY=12.18 EndZ=0
    g65: LineSegment StartX=26.82 StartY=12.18 StartZ=0 EndX=27.46 EndY=12.18 EndZ=0
    g66: LineSegment StartX=27.46 StartY=12.18 StartZ=0 EndX=27.46 EndY=12.82 EndZ=0
    g67: LineSegment StartX=27.46 StartY=12.82 StartZ=0 EndX=26.82 EndY=12.82 EndZ=0
    g68: LineSegment StartX=26.82 StartY=-12.18 StartZ=0 EndX=26.82 EndY=-12.82 EndZ=0
    g69: LineSegment StartX=26.82 StartY=-12.82 StartZ=0 EndX=27.46 EndY=-12.82 EndZ=0
    g70: LineSegment StartX=27.46 StartY=-12.82 StartZ=0 EndX=27.46 EndY=-12.18 EndZ=0
    g71: LineSegment StartX=27.46 StartY=-12.18 StartZ=0 EndX=26.82 EndY=-12.18 EndZ=0
    g72: LineSegment StartX=29.36 StartY=12.82 StartZ=0 EndX=29.36 EndY=12.18 EndZ=0
    g73: LineSegment StartX=29.36 StartY=12.18 StartZ=0 EndX=30 EndY=12.18 EndZ=0
    g74: LineSegment StartX=30 StartY=12.18 StartZ=0 EndX=30 EndY=12.82 EndZ=0
    g75: LineSegment StartX=30 StartY=12.82 StartZ=0 EndX=29.36 EndY=12.82 EndZ=0
    g76: LineSegment StartX=29.36 StartY=-12.18 StartZ=0 EndX=29.36 EndY=-12.82 EndZ=0
    g77: LineSegment StartX=29.36 StartY=-12.82 StartZ=0 EndX=30 EndY=-12.82 EndZ=0
    g78: LineSegment StartX=30 StartY=-12.82 StartZ=0 EndX=30 EndY=-12.18 EndZ=0
    g79: LineSegment StartX=30 StartY=-12.18 StartZ=0 EndX=29.36 EndY=-12.18 EndZ=0
    g80: LineSegment StartX=31.9 StartY=12.82 StartZ=0 EndX=31.9 EndY=12.18 EndZ=0
    g81: LineSegment StartX=31.9 StartY=12.18 StartZ=0 EndX=32.54 EndY=12.18 EndZ=0
    g82: LineSegment StartX=32.54 StartY=12.18 StartZ=0 EndX=32.54 EndY=12.82 EndZ=0
    g83: LineSegment StartX=32.54 StartY=12.82 StartZ=0 EndX=31.9 EndY=12.82 EndZ=0
    g84: LineSegment StartX=31.9 StartY=-12.18 StartZ=0 EndX=31.9 EndY=-12.82 EndZ=0
    g85: LineSegment StartX=31.9 StartY=-12.82 StartZ=0 EndX=32.54 EndY=-12.82 EndZ=0
    g86: LineSegment StartX=32.54 StartY=-12.82 StartZ=0 EndX=32.54 EndY=-12.18 EndZ=0
    g87: LineSegment StartX=32.54 StartY=-12.18 StartZ=0 EndX=31.9 EndY=-12.18 EndZ=0
    g88: LineSegment StartX=34.44 StartY=12.82 StartZ=0 EndX=34.44 EndY=12.18 EndZ=0
    g89: LineSegment StartX=34.44 StartY=12.18 StartZ=0 EndX=35.08 EndY=12.18 EndZ=0
    g90: LineSegment StartX=35.08 StartY=12.18 StartZ=0 EndX=35.08 EndY=12.82 EndZ=0
    g91: LineSegment StartX=35.08 StartY=12.82 StartZ=0 EndX=34.44 EndY=12.82 EndZ=0
    g92: LineSegment StartX=34.44 StartY=-12.18 StartZ=0 EndX=34.44 EndY=-12.82 EndZ=0
    g93: LineSegment StartX=34.44 StartY=-12.82 StartZ=0 EndX=35.08 EndY=-12.82 EndZ=0
    g94: LineSegment StartX=35.08 StartY=-12.82 StartZ=0 EndX=35.08 EndY=-12.18 EndZ=0
    g95: LineSegment StartX=35.08 StartY=-12.18 StartZ=0 EndX=34.44 EndY=-12.18 EndZ=0
    g96: LineSegment StartX=36.98 StartY=12.82 StartZ=0 EndX=36.98 EndY=12.18 EndZ=0
    g97: LineSegment StartX=36.98 StartY=12.18 StartZ=0 EndX=37.62 EndY=12.18 EndZ=0
    g98: LineSegment StartX=37.62 StartY=12.18 StartZ=0 EndX=37.62 EndY=12.82 EndZ=0
    g99: LineSegment StartX=37.62 StartY=12.82 StartZ=0 EndX=36.98 EndY=12.82 EndZ=0
    g100: LineSegment StartX=36.98 StartY=-12.18 StartZ=0 EndX=36.98 EndY=-12.82 EndZ=0
    g101: LineSegment StartX=36.98 StartY=-12.82 StartZ=0 EndX=37.62 EndY=-12.82 EndZ=0
    g102: LineSegment StartX=37.62 StartY=-12.82 StartZ=0 EndX=37.62 EndY=-12.18 EndZ=0
    g103: LineSegment StartX=37.62 StartY=-12.18 StartZ=0 EndX=36.98 EndY=-12.18 EndZ=0
    g104: LineSegment StartX=39.52 StartY=12.82 StartZ=0 EndX=39.52 EndY=12.18 EndZ=0
    g105: LineSegment StartX=39.52 StartY=12.18 StartZ=0 EndX=40.16 EndY=12.18 EndZ=0
    g106: LineSegment StartX=40.16 StartY=12.18 StartZ=0 EndX=40.16 EndY=12.82 EndZ=0
    g107: LineSegment StartX=40.16 StartY=12.82 StartZ=0 EndX=39.52 EndY=12.82 EndZ=0
    g108: LineSegment StartX=39.52 StartY=-12.18 StartZ=0 EndX=39.52 EndY=-12.82 EndZ=0
    g109: LineSegment StartX=39.52 StartY=-12.82 StartZ=0 EndX=40.16 EndY=-12.82 EndZ=0
    g110: LineSegment StartX=40.16 StartY=-12.82 StartZ=0 EndX=40.16 EndY=-12.18 EndZ=0
    g111: LineSegment StartX=40.16 StartY=-12.18 StartZ=0 EndX=39.52 EndY=-12.18 EndZ=0
    g112: LineSegment StartX=42.06 StartY=12.82 StartZ=0 EndX=42.06 EndY=12.18 EndZ=0
    g113: LineSegment StartX=42.06 StartY=12.18 StartZ=0 EndX=42.7 EndY=12.18 EndZ=0
    g114: LineSegment StartX=42.7 StartY=12.18 StartZ=0 EndX=42.7 EndY=12.82 EndZ=0
    g115: LineSegment StartX=42.7 StartY=12.82 StartZ=0 EndX=42.06 EndY=12.82 EndZ=0
    g116: LineSegment StartX=42.06 StartY=-12.18 StartZ=0 EndX=42.06 EndY=-12.82 EndZ=0
    g117: LineSegment StartX=42.06 StartY=-12.82 StartZ=0 EndX=42.7 EndY=-12.82 EndZ=0
    g118: LineSegment StartX=42.7 StartY=-12.82 StartZ=0 EndX=42.7 EndY=-12.18 EndZ=0
    g119: LineSegment StartX=42.7 StartY=-12.18 StartZ=0 EndX=42.06 EndY=-12.18 EndZ=0
  constraints (317):
    c: Coincident(g0,g1)
    c: Coincident(g1,g2)
    c: Coincident(g2,g3)
    c: Coincident(g3,g0)
    c: Vertical(g0)
    c: Vertical(g2)
    c: Horizontal(g1)
    c: Horizontal(g3)
    c: Coincident(g4,g5)
    c: Coincident(g5,g6)
    c: Coincident(g6,g7)
    c: Coincident(g7,g4)
    c: Vertical(g4)
    c: Vertical(g6)
    c: Horizontal(g5)
    c: Horizontal(g7)
    c: Equal(g1,g2)
    c: Equal(g1,g7)
    c: Equal(g6,g7)
    c: DistanceY(g6,g6) = 0.64
    c: DistanceX(g-1,g4) = 6.5
    c: DistanceY(g4,g0) = 25
    c: Symmetric(g4,g0,g-1)
    c: Coincident(g8,g9)
    c: Coincident(g16,g17)
    c: Coincident(g24,g25)
    c: Coincident(g32,g33)
    c: Coincident(g40,g41)
    c: Coincident(g48,g49)
    c: Coincident(g56,g57)
    c: Coincident(g64,g65)
    c: Coincident(g72,g73)
    c: Coincident(g80,g81)
    c: Coincident(g88,g89)
    c: Coincident(g96,g97)
    c: Coincident(g104,g105)
    c: Coincident(g112,g113)
    c: Coincident(g9,g10)
    c: Coincident(g17,g18)
    c: Coincident(g25,g26)
    c: Coincident(g33,g34)
    c: Coincident(g41,g42)
    c: Coincident(g49,g50)
    c: Coincident(g57,g58)
    c: Coincident(g65,g66)
    c: Coincident(g73,g74)
    c: Coincident(g81,g82)
    c: Coincident(g89,g90)
    c: Coincident(g97,g98)
    c: Coincident(g105,g106)
    c: Coincident(g113,g114)
    c: Coincident(g10,g11)
    c: Coincident(g18,g19)
    c: Coincident(g26,g27)
    c: Coincident(g34,g35)
    c: Coincident(g42,g43)
    c: Coincident(g50,g51)
    c: Coincident(g58,g59)
    c: Coincident(g66,g67)
    c: Coincident(g74,g75)
    c: Coincident(g82,g83)
    c: Coincident(g90,g91)
    c: Coincident(g98,g99)
    c: Coincident(g106,g107)
    c: Coincident(g114,g115)
    c: Coincident(g11,g8)
    c: Coincident(g19,g16)
    c: Coincident(g27,g24)
    c: Coincident(g35,g32)
    c: Coincident(g43,g40)
    c: Coincident(g51,g48)
    c: Coincident(g59,g56)
    c: Coincident(g67,g64)
    c: Coincident(g75,g72)
    c: Coincident(g83,g80)
    c: Coincident(g91,g88)
    c: Coincident(g99,g96)
    c: Coincident(g107,g104)
    c: Coincident(g115,g112)
    c: Vertical(g8)
    c: Vertical(g16)
    c: Vertical(g24)
    c: Vertical(g32)
    c: Vertical(g40)
    c: Vertical(g48)
    c: Vertical(g56)
    c: Vertical(g64)
    c: Vertical(g72)
    c: Vertical(g80)
    c: Vertical(g88)
    c: Vertical(g96)
    c: Vertical(g104)
    c: Vertical(g112)
    c: Vertical(g10)
    c: Vertical(g18)
    c: Vertical(g26)
    c: Vertical(g34)
    c: Vertical(g42)
    c: Vertical(g50)
    c: Vertical(g58)
    c: Vertical(g66)
    c: Vertical(g74)
    c: Vertical(g82)
    c: Vertical(g90)
    c: Vertical(g98)
    c: Vertical(g106)
    c: Vertical(g114)
    c: Horizontal(g9)
    c: Horizontal(g17)
    c: Horizontal(g25)
    c: Horizontal(g33)
    c: Horizontal(g41)
    c: Horizontal(g49)
    c: Horizontal(g57)
    c: Horizontal(g65)
    c: Horizontal(g73)
    c: Horizontal(g81)
    c: Horizontal(g89)
    c: Horizontal(g97)
    c: Horizontal(g105)
    c: Horizontal(g113)
    c: Horizontal(g11)
    c: Horizontal(g19)
    c: Horizontal(g27)
    c: Horizontal(g35)
    c: Horizontal(g43)
    c: Horizontal(g51)
    c: Horizontal(g59)
    c: Horizontal(g67)
    c: Horizontal(g75)
    c: Horizontal(g83)
    c: Horizontal(g91)
    c: Horizontal(g99)
    c: Horizontal(g107)
    c: Horizontal(g115)
    c: Coincident(g12,g13)
    c: Coincident(g20,g21)
    c: Coincident(g28,g29)
    c: Coincident(g36,g37)
    c: Coincident(g44,g45)
    c: Coincident(g52,g53)
    c: Coincident(g60,g61)
    c: Coincident(g68,g69)
    c: Coincident(g76,g77)
    c: Coincident(g84,g85)
    c: Coincident(g92,g93)
    c: Coincident(g100,g101)
    c: Coincident(g108,g109)
    c: Coincident(g116,g117)
    c: Coincident(g13,g14)
    c: Coincident(g21,g22)
    c: Coincident(g29,g30)
    c: Coincident(g37,g38)
    c: Coincident(g45,g46)
    c: Coincident(g53,g54)
    c: Coincident(g61,g62)
    c: Coincident(g69,g70)
    c: Coincident(g77,g78)
    c: Coincident(g85,g86)
    c: Coincident(g93,g94)
    c: Coincident(g101,g102)
    c: Coincident(g109,g110)
    c: Coincident(g117,g118)
    c: Coincident(g14,g15)
    c: Coincident(g22,g23)
    c: Coincident(g30,g31)
    c: Coincident(g38,g39)
    c: Coincident(g46,g47)
    c: Coincident(g54,g55)
    c: Coincident(g62,g63)
    c: Coincident(g70,g71)
    c: Coincident(g78,g79)
    c: Coincident(g86,g87)
    c: Coincident(g94,g95)
    c: Coincident(g102,g103)
    c: Coincident(g110,g111)
    c: Coincident(g118,g119)
    c: Coincident(g15,g12)
    c: Coincident(g23,g20)
    c: Coincident(g31,g28)
    c: Coincident(g39,g36)
    c: Coincident(g47,g44)
    c: Coincident(g55,g52)
    c: Coincident(g63,g60)
    c: Coincident(g71,g68)
    c: Coincident(g79,g76)
    c: Coincident(g87,g84)
    c: Coincident(g95,g92)
    c: Coincident(g103,g100)
    c: Coincident(g111,g108)
    c: Coincident(g119,g116)
    c: Vertical(g12)
    c: Vertical(g20)
    c: Vertical(g28)
    c: Vertical(g36)
    c: Vertical(g44)
    c: Vertical(g52)
    c: Vertical(g60)
    c: Vertical(g68)
    c: Vertical(g76)
    c: Vertical(g84)
    c: Vertical(g92)
    c: Vertical(g100)
    c: Vertical(g108)
    c: Vertical(g116)
    c: Vertical(g14)
    c: Vertical(g22)
    c: Vertical(g30)
    c: Vertical(g38)
    c: Vertical(g46)
    c: Vertical(g54)
    c: Vertical(g62)
    c: Vertical(g70)
    c: Vertical(g78)
    c: Vertical(g86)
    c: Vertical(g94)
    c: Vertical(g102)
    c: Vertical(g110)
    c: Vertical(g118)
    c: Horizontal(g13)
    c: Horizontal(g21)
    c: Horizontal(g29)
    c: Horizontal(g37)
    c: Horizontal(g45)
    c: Horizontal(g53)
    c: Horizontal(g61)
    c: Horizontal(g69)
    c: Horizontal(g77)
    c: Horizontal(g85)
    c: Horizontal(g93)
    c: Horizontal(g101)
    c: Horizontal(g109)
    c: Horizontal(g117)
    c: Horizontal(g15)
    c: Horizontal(g23)
    c: Horizontal(g31)
    c: Horizontal(g39)
    c: Horizontal(g47)
    c: Horizontal(g55)
    c: Horizontal(g63)
    c: Horizontal(g71)
    c: Horizontal(g79)
    c: Horizontal(g87)
    c: Horizontal(g95)
    c: Horizontal(g103)
    c: Horizontal(g111)
    c: Horizontal(g119)
    c: Equal(g9,g10)
    c: Equal(g17,g18)
    c: Equal(g25,g26)
    c: Equal(g33,g34)
    c: Equal(g41,g42)
    c: Equal(g49,g50)
    c: Equal(g57,g58)
    c: Equal(g65,g66)
    c: Equal(g73,g74)
    c: Equal(g81,g82)
    c: Equal(g89,g90)
    c: Equal(g97,g98)
    c: Equal(g105,g106)
    c: Equal(g113,g114)
    c: Equal(g9,g15)
    c: Equal(g17,g23)
    c: Equal(g25,g31)
    c: Equal(g33,g39)
    c: Equal(g41,g47)
    c: Equal(g49,g55)
    c: Equal(g57,g63)
    c: Equal(g65,g71)
    c: Equal(g73,g79)
    c: Equal(g81,g87)
    c: Equal(g89,g95)
    c: Equal(g97,g103)
    c: Equal(g105,g111)
    c: Equal(g113,g119)
    c: Equal(g14,g15)
    c: Equal(g22,g23)
    c: Equal(g30,g31)
    c: Equal(g38,g39)
    c: Equal(g46,g47)
    c: Equal(g54,g55)
    c: Equal(g62,g63)
    c: Equal(g70,g71)
    c: Equal(g78,g79)
    c: Equal(g86,g87)
    c: Equal(g94,g95)
    c: Equal(g102,g103)
    c: Equal(g110,g111)
    c: Equal(g118,g119)
    c: DistanceY(g14,g14) = 0.64
    c: DistanceY(g22,g22) = 0.64
    c: DistanceY(g30,g30) = 0.64
    c: DistanceY(g38,g38) = 0.64
    c: DistanceY(g46,g46) = 0.64
    c: DistanceY(g54,g54) = 0.64
    c: DistanceY(g62,g62) = 0.64
    c: DistanceY(g70,g70) = 0.64
    c: DistanceY(g78,g78) = 0.64
    c: DistanceY(g86,g86) = 0.64
    c: DistanceY(g94,g94) = 0.64
    c: DistanceY(g102,g102) = 0.64
    c: DistanceY(g110,g110) = 0.64
    c: DistanceY(g118,g118) = 0.64
    c: DistanceY(g12,g8) = 25
    c: DistanceY(g20,g16) = 25
    c: DistanceY(g28,g24) = 25
    c: DistanceY(g36,g32) = 25
    c: DistanceY(g44,g40) = 25
    c: DistanceY(g52,g48) = 25
    c: DistanceY(g60,g56) = 25
    c: DistanceY(g68,g64) = 25
    c: DistanceY(g76,g72) = 25
    c: DistanceY(g84,g80) = 25
    c: DistanceY(g92,g88) = 25
    c: DistanceY(g100,g96) = 25
    c: DistanceY(g108,g104) = 25
    c: DistanceY(g116,g112) = 25
FEATURE [PartDesign::Pad] Pad032
  BaseFeature = -> Pad031
  Direction = (0,0,1)
  Length = 8.5
  Length2 = 10
  Profile = -> Sketch021
  ReferenceAxis = -> Sketch021 [N_Axis]
  Refine = true
  Reversed = true
  Suppressed = false
  Type = 0
FEATURE [PartDesign::Body] Body008  label="esp_new_mdl"
  AllowCompound = false
  Group = -> [Sketch016,Pad001,Sketch017,Pad003,Sketch018,Pad029,Sketch004,Pad030,Sketch019,Pad006,Sketch020,Pad031,Sketch021,Pad032]
  Origin = -> Origin008
  Placement = pos=(-1.28e-14,0,0) rot=(-0.57735,-0.57735,0.57735;0rad)
  Tip = -> Pad032
FEATURE [Image::ImagePlane] esp_new
  Placement = pos=(-0.5,2.5,0) rot=(0,0,1;1.5708rad)
  XSize = 91.3875
  YSize = 91.3875
FEATURE [Image::ImagePlane] encoder
  Placement = pos=(-7,-2,0) rot=(0,0,1;0rad)
  XSize = 84.6872
  YSize = 50.0838
FEATURE [PartDesign::Pad] Pad
  Direction = (0,0,1)
  Length = 67
  Length2 = 10
  Profile = -> Sketch005
  ReferenceAxis = -> Sketch005 [N_Axis]
  Refine = true
  Suppressed = false
  Type = 0
FEATURE [PartDesign::Body] Body004  label="akku"
  AllowCompound = false
  Group = -> [Sketch005,Pad]
  Origin = -> Origin004
  Tip = -> Pad
COMPONENT P13 — recipe-attached ("link_display", modeled in this document).
Construction recipe (the document's own serialized feature program — sketch geometry with constraints, then the solid features built on it; lengths are millimeters unless a unit is written):

FEATURE [PartDesign::SubShapeBinder] Binder014
  BindCopyOnChange = 0
  BindMode = 0
  ClaimChildren = false
  Context = -> Array001 [Binder014.]
  Fuse = false
  MakeFace = true
  Offset = 5
  OffsetFill = false
  OffsetIntersection = false
  OffsetJoinType = 0
  OffsetOpenResult = false
  PartialLoad = false
  Refine = true
  Relative = true
  Support = -> [Cut[Edge167,Edge166,Edge169,Edge168]]
  _Version = 2
FEATURE [PartDesign::Pad] Pad
  Direction = (0.612372,0.612372,0.5)
  Length = 10
  Length2 = 10
  Profile = -> Binder014
  Refine = true
  Suppressed = false
  Type = 0
FEATURE [PartDesign::Body] Body001  label="Dispcut"
  AllowCompound = false
  Group = -> [Binder014,Pad]
  Origin = -> Origin001
  Tip = -> Pad
COMPONENT P14 — same part as P12; its construction recipe is shown at P12.
COMPONENT P15 — same part as P12; its construction recipe is shown at P12.
COMPONENT P16 — same part as P12; its construction recipe is shown at P12.
COMPONENT P17 — same part as P12; its construction recipe is shown at P12.
COMPONENT P18 — same part as P12; its construction recipe is shown at P12.
COMPONENT P19 — recipe-attached ("Link007", a linked part whose construction recipe lives in a companion FreeCAD document of the same project; that document's serialized recipe follows).
Construction recipe (the companion document, serialized — sketch geometry with constraints, then the solid features built on it; lengths are millimeters unless a unit is written):

FCSTD DOCUMENT  (FreeCAD 1.0R38641 +1 (Git))
Label: feet2
License: All rights reserved
LicenseURL: https://en.wikipedia.org/wiki/All_rights_reserved
objects: Sketcher::SketchObject×13, PartDesign::Pad×8, PartDesign::Pocket×6, PartDesign::Body×5, Part::Mirroring×3, Part::MultiFuse×3, PartDesign::PolarPattern×2, Part::Cut×2, Part::Box×1, PartDesign::FeatureBase×1, PartDesign::SubShapeBinder×1, Part::Compound×1, Mesh::Feature×1
note: 90 computed .brp shape members not serialized (recipe doc carries the construction recipe); baked Part::Feature solids carry a one-line shape summary decoded from their .brp

FEATURE [Sketcher::SketchObject] Sketch003
  ArcFitTolerance = 1e-06
  AttachmentSupport = -> [XZ_Plane001]
  FullyConstrained = true
  MakeInternals = false
  MapMode = 5
  Placement = pos=(0,0,0) rot=(1,0,0;1.5708rad)
  sketch-geometry (13):
    g0: LineSegment StartX=-20 StartY=-1.5 StartZ=0 EndX=-18.2679 EndY=1.5 EndZ=0
    g1: LineSegment StartX=-18.2679 StartY=1.5 StartZ=0 EndX=0 EndY=1.5 EndZ=0
    g2: LineSegment StartX=-2e-16 StartY=-1.5 StartZ=0 EndX=-12 EndY=-1.5 EndZ=0
    g3: LineSegment StartX=-2e-16 StartY=-1.5 StartZ=0 EndX=0.75 EndY=-1.5 EndZ=0
    g4: LineSegment StartX=1.5 StartY=-0.75 StartZ=0 EndX=1.5 EndY=0 EndZ=0
    g5: ArcOfCircle CenterX=0 CenterY=0 CenterZ=0 NormalX=0 NormalY=0 NormalZ=1 AngleXU=0 Radius=1.5 StartAngle=0 EndAngle=1.5708
    g6: ArcOfCircle [constr] CenterX=0.75 CenterY=-0.75 CenterZ=0 NormalX=0 NormalY=0 NormalZ=1 AngleXU=0 Radius=0.75 StartAngle=4.71239 EndAngle=6.28319
    g7: GeomPoint [constr] X=1.5 Y=-1.5 Z=0
    g8: LineSegment StartX=0.75 StartY=-1.5 StartZ=0 EndX=1.5 EndY=-0.75 EndZ=0
    g9: LineSegment StartX=-16 StartY=-1.5 StartZ=0 EndX=-15 EndY=-0.5 EndZ=0
    g10: LineSegment StartX=-15 StartY=-0.5 StartZ=0 EndX=-13 EndY=-0.5 EndZ=0
    g11: LineSegment StartX=-13 StartY=-0.5 StartZ=0 EndX=-12 EndY=-1.5 EndZ=0
    g12: LineSegment StartX=-16 StartY=-1.5 StartZ=0 EndX=-20 EndY=-1.5 EndZ=0
  constraints (35):
    c: Coincident(g0,g1)
    c: Horizontal(g1)
    c: Coincident(g12,g0)
    c: Horizontal(g2)
    c: Symmetric(g2,g1,g-1)
    c: DistanceX(g12,g2) = 20
    c: DistanceY(g2,g1) = 3
    c: Angle(g2,g0) = 1.0472
    c: Coincident(g2,g3)
    c: Horizontal(g3)
    c: PointOnObject(g4,g-1)
    c: Vertical(g4)
    c: Coincident(g5,g-1)
    c: Coincident(g5,g4)
    c: Tangent(g5,g1) = 1.5708
    c: PointOnObject(g7,g3)
    c: PointOnObject(g7,g4)
    c: Tangent(g3,g6) = -1.5708
    c: Tangent(g4,g6) = -1.5708
    c: Coincident(g8,g3)
    c: Coincident(g8,g4)
    c: DistanceX(g3,g3) = 0.75
    c: PointOnObject(g9,g12)
    c: Coincident(g9,g10)
    c: Horizontal(g10)
    c: Coincident(g10,g11)
    c: DistanceY(g11,g10) = 1
    c: DistanceX(g10,g10) = 2
    c: Angle(g11,g2) = 0.785398
    c: Angle(g9,g2) = 2.35619
    c: DistanceX(g0,g9) = 4
    c: Coincident(g2,g11)
    c: PointOnObject(g12,g9)
    c: Horizontal(g12)
    c: Horizontal(g9,g2)
FEATURE [PartDesign::Pad] Pad001
  Direction = (0,-1,2e-16)
  Length = 5
  Length2 = 10
  Placement = pos=(0,0,0) rot=(1,0,0;1.5708rad)
  Profile = -> Sketch003
  ReferenceAxis = -> Sketch003 [N_Axis]
  Refine = true
  Suppressed = false
  Type = 0
FEATURE [Sketcher::SketchObject] Sketch004
  ArcFitTolerance = 1e-06
  AttachmentOffset = pos=(0,0,5) rot=(0,0,1;0rad)
  AttachmentSupport = -> [XZ_Plane001]
  FullyConstrained = true
  MakeInternals = false
  MapMode = 5
  Placement = pos=(0,-5,1.1e-15) rot=(1,0,0;1.5708rad)
  sketch-geometry (4):
    g0: ArcOfCircle CenterX=0 CenterY=0 CenterZ=0 NormalX=0 NormalY=0 NormalZ=1 AngleXU=0 Radius=1 StartAngle=4.71239 EndAngle=7.85398
    g1: ArcOfCircle CenterX=-5 CenterY=-2e-16 CenterZ=0 NormalX=0 NormalY=0 NormalZ=1 AngleXU=0 Radius=1 StartAngle=1.5708 EndAngle=4.71239
    g2: LineSegment StartX=-2e-16 StartY=-1 StartZ=0 EndX=-5 EndY=-1 EndZ=0
    g3: LineSegment StartX=3e-16 StartY=1 StartZ=0 EndX=-5 EndY=1 EndZ=0
  constraints (9):
    c: Tangent(g0,g2) = 1.5708
    c: Tangent(g0,g3) = -1.5708
    c: Tangent(g1,g2) = 1.5708
    c: Tangent(g1,g3) = -1.5708
    c: Equal(g0,g1)
    c: Horizontal(g3)
    c: Radius(g0) = 1
    c: Coincident(g0,g-1)
    c: DistanceX(g1,g0) = 5
FEATURE [PartDesign::Pocket] Pocket001
  BaseFeature = -> Pad001
  Direction = (0,1,-2e-16)
  Length = 1.5
  Length2 = 5
  Placement = pos=(0,0,0) rot=(1,0,0;1.5708rad)
  Profile = -> Sketch004
  ReferenceAxis = -> Sketch004 [N_Axis]
  Refine = true
  Suppressed = false
  TaperAngle = -30
  Type = 0
FEATURE [PartDesign::Body] Body001  label="A001"
  AllowCompound = false
  Group = -> [Sketch003,Pad001,Sketch004,Pocket001]
  Origin = -> Origin001
  Tip = -> Pocket001
FEATURE [Sketcher::SketchObject] Sketch005
  ArcFitTolerance = 1e-06
  AttachmentSupport = -> [XZ_Plane002]
  FullyConstrained = true
  MakeInternals = false
  MapMode = 5
  Placement = pos=(0,0,0) rot=(1,0,0;1.5708rad)
  sketch-geometry (14):
    g0: LineSegment StartX=-20.2 StartY=-1.5 StartZ=0 EndX=-18.3525 EndY=1.7 EndZ=0
    g1: LineSegment StartX=-18.3525 StartY=1.7 StartZ=0 EndX=-2.5815 EndY=1.7 EndZ=0
    g2: LineSegment StartX=-2.5815 StartY=1.7 StartZ=0 EndX=-3.85167 EndY=3.9 EndZ=0
    g3: LineSegment StartX=-3.85167 StartY=3.9 StartZ=0 EndX=-0.651666 EndY=3.9 EndZ=0
    g4: LineSegment StartX=-0.651666 StartY=3.9 StartZ=0 EndX=0.618505 EndY=1.7 EndZ=0
    g5: LineSegment StartX=0.618505 StartY=1.7 StartZ=0 EndX=5.5 EndY=1.7 EndZ=0
    g6: LineSegment StartX=5.5 StartY=1.7 StartZ=0 EndX=5.5 EndY=-1.5 EndZ=0
    g7: LineSegment StartX=5.5 StartY=-1.5 StartZ=0 EndX=8 EndY=-1.5 EndZ=0
    g8: LineSegment StartX=8 StartY=-1.5 StartZ=0 EndX=8 EndY=4.5 EndZ=0
    g9: LineSegment StartX=8 StartY=4.5 StartZ=0 EndX=-22 EndY=4.5 EndZ=0
    g10: LineSegment [constr] StartX=0 StartY=0 StartZ=0 EndX=-2.25167 EndY=3.9 EndZ=0
    g11: Circle [constr] CenterX=0 CenterY=0 CenterZ=0 NormalX=0 NormalY=0 NormalZ=1 AngleXU=0 Radius=1.80902
    g12: LineSegment StartX=-20.2 StartY=-1.5 StartZ=0 EndX=-22 EndY=-1.5 EndZ=0
    g13: LineSegment StartX=-22 StartY=-1.5 StartZ=0 EndX=-22 EndY=4.5 EndZ=0
  constraints (40):
    c: Coincident(g0,g1)
    c: Horizontal(g1)
    c: Coincident(g1,g2)
    c: Coincident(g2,g3)
    c: Horizontal(g3)
    c: Coincident(g3,g4)
    c: Coincident(g4,g5)
    c: Horizontal(g5)
    c: Coincident(g5,g6)
    c: Vertical(g6)
    c: Coincident(g6,g7)
    c: Horizontal(g7)
    c: Coincident(g7,g8)
    c: Vertical(g8)
    c: Coincident(g8,g9)
    c: Horizontal(g9)
    c: Parallel(g2,g4)
    c: Angle(g2,g1) = 1.0472
    c: DistanceX(g1,g4) = 3.2
    c: Horizontal(g4,g1)
    c: Horizontal(g6,g0)
    c: Angle(g0,g-1) = 2.0944
    c: DistanceY(g6) = -1.5
    c: DistanceY(g6,g6) = 3.2
    c: DistanceY(g8,g8) = 6
    c: Coincident(g10,g-1)
    c: Symmetric(g3,g3,g10)
    c: Parallel(g10,g4)
    c: DistanceX(g0) = -20.2
    c: Coincident(g11,g10)
    c: PointOnObject(g4,g11)
    c: DistanceY(g3,g8) = 0.6
    c: DistanceX(g5) = 5.5
    c: Coincident(g0,g12)
    c: Horizontal(g12)
    c: Coincident(g12,g13)
    c: Coincident(g13,g9)
    c: Vertical(g13)
    c: DistanceX(g9,g9) = 30
    c: DistanceX(g12) = -22
FEATURE [PartDesign::Pad] Pad002
  Direction = (0,-1,2e-16)
  Length = 5.2
  Length2 = 10
  Placement = pos=(0,0,0) rot=(1,0,0;1.5708rad)
  Profile = -> Sketch005
  ReferenceAxis = -> Sketch005 [N_Axis]
  Refine = true
  Suppressed = false
  Type = 0
FEATURE [Sketcher::SketchObject] Sketch006
  ArcFitTolerance = 1e-06
  AttachmentOffset = pos=(0,0,5.2) rot=(0,0,1;0rad)
  AttachmentSupport = -> [XZ_Plane002]
  FullyConstrained = true
  MakeInternals = false
  MapMode = 5
  Placement = pos=(0,-5.2,1.2e-15) rot=(1,0,0;1.5708rad)
  sketch-geometry (1):
    g0: Circle CenterX=0 CenterY=0 CenterZ=0 NormalX=0 NormalY=0 NormalZ=1 AngleXU=0 Radius=1.05
  constraints (2):
    c: Diameter(g0) = 2.1
    c: Coincident(g0,g-1)
FEATURE [PartDesign::Pad] Pad003
  BaseFeature = -> Pad002
  Direction = (0,-1,2e-16)
  Length = 1.6
  Length2 = 10
  Placement = pos=(0,0,0) rot=(1,0,0;1.5708rad)
  Profile = -> Sketch006
  ReferenceAxis = -> Sketch006 [N_Axis]
  Refine = true
  Reversed = true
  Suppressed = false
  TaperAngle = -30
  Type = 0
FEATURE [Sketcher::SketchObject] Sketch007
  ArcFitTolerance = 1e-06
  AttachmentOffset = pos=(0,0,5.2) rot=(0,0,1;0rad)
  AttachmentSupport = -> [XZ_Plane002]
  FullyConstrained = true
  MakeInternals = false
  MapMode = 5
  Placement = pos=(0,-5.2,1.2e-15) rot=(1,0,0;1.5708rad)
  sketch-geometry (4):
    g0: LineSegment StartX=-22 StartY=4.5 StartZ=0 EndX=-22 EndY=-1.5 EndZ=0
    g1: LineSegment StartX=-22 StartY=-1.5 StartZ=0 EndX=8 EndY=-1.5 EndZ=0
    g2: LineSegment StartX=8 StartY=-1.5 StartZ=0 EndX=8 EndY=4.5 EndZ=0
    g3: LineSegment StartX=8 StartY=4.5 StartZ=0 EndX=-22 EndY=4.5 EndZ=0
  constraints (12):
    c: Coincident(g0,g1)
    c: Coincident(g1,g2)
    c: Coincident(g2,g3)
    c: Coincident(g3,g0)
    c: Vertical(g0)
    c: Vertical(g2)
    c: Horizontal(g1)
    c: Horizontal(g3)
    c: DistanceX(g3,g3) = 30
    c: DistanceY(g0,g0) = 6
    c: DistanceX(g0) = -22
    c: DistanceY(g1) = -1.5
FEATURE [PartDesign::Pad] Pad004
  BaseFeature = -> Pad003
  Direction = (0,-1,2e-16)
  Length = 4.8
  Length2 = 10
  Placement = pos=(0,0,0) rot=(1,0,0;1.5708rad)
  Profile = -> Sketch007
  ReferenceAxis = -> Sketch007 [N_Axis]
  Refine = true
  Suppressed = false
  Type = 0
FEATURE [PartDesign::Body] Body002  label="A002"
  AllowCompound = true
  Group = -> [Sketch005,Pad002,Sketch006,Pad003,Sketch007,Pad004]
  Origin = -> Origin002
  Tip = -> Pad004
FEATURE [Sketcher::SketchObject] Sketch008
  ArcFitTolerance = 1e-06
  AttachmentSupport = -> [XZ_Plane003]
  FullyConstrained = true
  MakeInternals = false
  MapMode = 5
  Placement = pos=(0,0,0) rot=(1,0,0;1.5708rad)
  sketch-geometry (4):
    g0: LineSegment StartX=-20 StartY=-2.5 StartZ=0 EndX=-17.1132 EndY=2.5 EndZ=0
    g1: LineSegment StartX=-17.1132 StartY=2.5 StartZ=0 EndX=0 EndY=2.5 EndZ=0
    g2: LineSegment StartX=-5e-16 StartY=-2.5 StartZ=0 EndX=-20 EndY=-2.5 EndZ=0
    g3: ArcOfCircle CenterX=0 CenterY=0 CenterZ=0 NormalX=0 NormalY=0 NormalZ=1 AngleXU=0 Radius=2.5 StartAngle=4.71239 EndAngle=7.85398
  constraints (11):
    c: Coincident(g0,g1)
    c: Horizontal(g1)
    c: Horizontal(g2)
    c: DistanceX(g0,g2) = 20
    c: Angle(g2,g0) = 1.0472
    c: PointOnObject(g2,g-2)
    c: Coincident(g2,g0)
    c: Coincident(g3,g-1)
    c: Tangent(g3,g1) = 1.5708
    c: Coincident(g3,g2)
    c: Radius(g3) = 2.5
FEATURE [PartDesign::Pad] Pad005
  Direction = (0,-1,2e-16)
  Length = 5
  Length2 = 10
  Placement = pos=(0,0,0) rot=(1,0,0;1.5708rad)
  Profile = -> Sketch008
  ReferenceAxis = -> Sketch008 [N_Axis]
  Refine = true
  Suppressed = false
  Type = 0
FEATURE [Sketcher::SketchObject] Sketch009
  ArcFitTolerance = 1e-06
  AttachmentOffset = pos=(0,0,5) rot=(0,0,1;0rad)
  AttachmentSupport = -> [XZ_Plane003]
  FullyConstrained = true
  MakeInternals = false
  MapMode = 5
  Placement = pos=(0,-5,1.1e-15) rot=(1,0,0;1.5708rad)
  sketch-geometry (7):
    g0: LineSegment StartX=1.51554 StartY=-0.875 StartZ=0 EndX=1.51554 EndY=0.875 EndZ=0
    g1: LineSegment StartX=1.51554 StartY=0.875 StartZ=0 EndX=-2e-16 EndY=1.75 EndZ=0
    g2: LineSegment StartX=-2e-16 StartY=1.75 StartZ=0 EndX=-1.51554 EndY=0.875 EndZ=0
    g3: LineSegment StartX=-1.51554 StartY=0.875 StartZ=0 EndX=-1.51554 EndY=-0.875 EndZ=0
    g4: LineSegment StartX=-1.51554 StartY=-0.875 StartZ=0 EndX=0 EndY=-1.75 EndZ=0
    g5: LineSegment StartX=0 StartY=-1.75 StartZ=0 EndX=1.51554 EndY=-0.875 EndZ=0
    g6: Circle [constr] CenterX=0 CenterY=0 CenterZ=0 NormalX=0 NormalY=0 NormalZ=1 AngleXU=0 Radius=1.75
  constraints (17):
    c: Coincident(g0,g1)
    c: Coincident(g1,g2)
    c: Coincident(g2,g3)
    c: Coincident(g3,g4)
    c: Coincident(g4,g5)
    c: Coincident(g5,g0)
    c: Equal(g0, g1-g5) x5
    c: PointOnObject(g0,g6)
    c: PointOnObject(g1,g6)
    c: PointOnObject(g2,g6)
    c: PointOnObject(g3,g6)
    c: PointOnObject(g4,g6)
    c: PointOnObject(g5,g6)
    c: Coincident(g6,g-1)
    c: Diameter(g6) = 3.5
    c: Vertical(g3)
    c: DistanceX(g3,g0) = 3.03109
FEATURE [PartDesign::Pocket] Pocket002
  BaseFeature = -> Pad005
  Direction = (0,1,-2e-16)
  Length = 1.5
  Length2 = 5
  Placement = pos=(0,0,0) rot=(1,0,0;1.5708rad)
  Profile = -> Sketch009
  ReferenceAxis = -> Sketch009 [N_Axis]
  Refine = true
  Suppressed = false
  Type = 1
FEATURE [Sketcher::SketchObject] Sketch010
  ArcFitTolerance = 1e-06
  AttachmentSupport = -> [XZ_Plane004]
  FullyConstrained = true
  MakeInternals = false
  MapMode = 5
  Placement = pos=(0,0,0) rot=(1,0,0;1.5708rad)
  sketch-geometry (17):
    g0: LineSegment StartX=8 StartY=-2.5 StartZ=0 EndX=8 EndY=3.5 EndZ=0
    g1: LineSegment StartX=8 StartY=3.5 StartZ=0 EndX=-27 EndY=3.5 EndZ=0
    g2: LineSegment StartX=-27 StartY=3.5 StartZ=0 EndX=-27 EndY=-2.5 EndZ=0
    g3: LineSegment StartX=-27 StartY=-2.5 StartZ=0 EndX=-21.5588 EndY=-2.5 EndZ=0
    g4: LineSegment StartX=-21.5588 StartY=-2.5 StartZ=0 EndX=-20.1155 EndY=0 EndZ=0
    g5: LineSegment StartX=-20.1155 StartY=0 StartZ=0 EndX=-19.1155 EndY=0 EndZ=0
    g6: LineSegment StartX=-19.1155 StartY=0 StartZ=0 EndX=-17.4412 EndY=2.9 EndZ=0
    g7: LineSegment StartX=-17.4412 StartY=2.9 StartZ=0 EndX=1.55885 EndY=2.9 EndZ=0
    g8: LineSegment StartX=4.67654 StartY=-2.5 StartZ=0 EndX=8 EndY=-2.5 EndZ=0
    g9: LineSegment [constr] StartX=4.67654 StartY=-2.5 StartZ=0 EndX=0 EndY=-2.5 EndZ=0
    g10: LineSegment [constr] StartX=1.21244 StartY=2.9 StartZ=0 EndX=4.33013 EndY=-2.5 EndZ=0
    g11: LineSegment StartX=1.55885 StartY=2.9 StartZ=0 EndX=3.4641 EndY=-0.4 EndZ=0
    g12: LineSegment [constr] StartX=3.4641 StartY=-0.4 StartZ=0 EndX=4.67654 EndY=-2.5 EndZ=0
    g13: LineSegment StartX=3.4641 StartY=-0.4 StartZ=0 EndX=3.4641 EndY=-1 EndZ=0
    g14: LineSegment StartX=3.4641 StartY=-1 StartZ=0 EndX=4.33013 EndY=-2.5 EndZ=0
    g15: LineSegment StartX=4.33013 StartY=-2.5 StartZ=0 EndX=4.67654 EndY=-2.5 EndZ=0
    g16: Circle CenterX=0 CenterY=0 CenterZ=0 NormalX=0 NormalY=0 NormalZ=1 AngleXU=0 Radius=1.4
  constraints (50):
    c: Coincident(g0,g1)
    c: Coincident(g1,g2)
    c: Horizontal(g1)
    c: Vertical(g0)
    c: Vertical(g2)
    c: DistanceY(g0) = -2.5
    c: DistanceY(g0,g0) = 6
    c: Coincident(g2,g3)
    c: Horizontal(g3)
    c: Coincident(g3,g4)
    c: PointOnObject(g4,g-1)
    c: Coincident(g4,g5)
    c: PointOnObject(g5,g-1)
    c: Coincident(g5,g6)
    c: Coincident(g6,g7)
    c: Horizontal(g7)
    c: Coincident(g7,g11)
    c: DistanceY(g7) = 2.9
    c: Coincident(g8,g12)
    c: Coincident(g8,g0)
    c: Horizontal(g8)
    c: Angle(g6,g7) = 2.0944
    c: Horizontal(g3,g12)
    c: DistanceX(g7,g7) = 19
    c: DistanceX(g5,g5) = 1
    c: DistanceX(g1,g1) = 35
    c: DistanceX(g0) = 8
    c: DistanceY(g7,g0) = 0.6
    c: Coincident(g9,g12)
    c: Horizontal(g9)
    c: PointOnObject(g10,g7)
    c: PointOnObject(g10,g9)
    c: Coincident(g11,g12)
    c: Parallel(g10,g11)
    c: Parallel(g10,g12)
    c: Coincident(g13,g11)
    c: PointOnObject(g13,g10)
    c: Coincident(g14,g13)
    c: Coincident(g14,g10)
    c: Coincident(g15,g10)
    c: Coincident(g15,g8)
    c: Vertical(g13)
    c: Angle(g7,g11) = 2.0944
    c: DistanceY(g13) = -1
    c: Parallel(g4,g6)
    c: PointOnObject(g9,g-2)
    c: Distance(g-1,g10) = 2.5
    c: Distance(g-1,g11) = 2.8
    c: Coincident(g16,g-1)
    c: Diameter(g16) = 2.8
FEATURE [PartDesign::Pad] Pad006
  Direction = (0,-1,2e-16)
  Length = 5.2
  Length2 = 10
  Placement = pos=(0,0,0) rot=(1,0,0;1.5708rad)
  Profile = -> Sketch010
  ReferenceAxis = -> Sketch010 [N_Axis]
  Refine = true
  Suppressed = false
  Type = 0
FEATURE [Sketcher::SketchObject] Sketch012
  ArcFitTolerance = 1e-06
  AttachmentOffset = pos=(0,0,5.2) rot=(0,0,1;0rad)
  AttachmentSupport = -> [XZ_Plane004]
  FullyConstrained = true
  MakeInternals = false
  MapMode = 5
  Placement = pos=(0,-5.2,1.2e-15) rot=(1,0,0;1.5708rad)
  sketch-geometry (4):
    g0: LineSegment StartX=-27 StartY=3.5 StartZ=0 EndX=-27 EndY=-2.5 EndZ=0
    g1: LineSegment StartX=-27 StartY=-2.5 StartZ=0 EndX=8 EndY=-2.5 EndZ=0
    g2: LineSegment StartX=8 StartY=-2.5 StartZ=0 EndX=8 EndY=3.5 EndZ=0
    g3: LineSegment StartX=8 StartY=3.5 StartZ=0 EndX=-27 EndY=3.5 EndZ=0
  constraints (12):
    c: Coincident(g0,g1)
    c: Coincident(g1,g2)
    c: Coincident(g2,g3)
    c: Coincident(g3,g0)
    c: Vertical(g0)
    c: Vertical(g2)
    c: Horizontal(g1)
    c: Horizontal(g3)
    c: DistanceX(g3,g3) = 35
    c: DistanceY(g0,g0) = 6
    c: DistanceY(g1) = -2.5
    c: DistanceX(g2) = 8
FEATURE [Part::Box] Box  label="Cube"
  AttacherType = Attacher::AttachEngine3D
  Height = 6
  Length = 35
  Placement = pos=(-27,-10,-2.5) rot=(0,0,1;0rad)
  Width = 10
FEATURE [Sketcher::SketchObject] Sketch016
  ArcFitTolerance = 1e-06
  AttachmentSupport = -> [XY_Plane003]
  FullyConstrained = true
  MakeInternals = false
  MapMode = 5
  sketch-geometry (8):
    g0: ArcOfCircle CenterX=-14 CenterY=0 CenterZ=0 NormalX=0 NormalY=0 NormalZ=1 AngleXU=0 Radius=1.5 StartAngle=1.5708 EndAngle=4.71239
    g1: LineSegment StartX=4 StartY=1 StartZ=0 EndX=4 EndY=-1 EndZ=0
    g2: LineSegment StartX=-4 StartY=1 StartZ=0 EndX=4 EndY=1 EndZ=0
    g3: LineSegment StartX=-14 StartY=1.5 StartZ=0 EndX=-7 EndY=1.5 EndZ=0
    g4: LineSegment StartX=-7 StartY=1.5 StartZ=0 EndX=-4 EndY=1 EndZ=0
    g5: LineSegment StartX=-14 StartY=-1.5 StartZ=0 EndX=-7 EndY=-1.5 EndZ=0
    g6: LineSegment StartX=-7 StartY=-1.5 StartZ=0 EndX=-4 EndY=-1 EndZ=0
    g7: LineSegment StartX=-4 StartY=-1 StartZ=0 EndX=4 EndY=-1 EndZ=0
  constraints (25):
    c: DistanceY(g7) = -1
    c: DistanceX(g5) = -14
    c: Coincident(g5,g0) = -1.5708
    c: Coincident(g0,g3) = 1.5708
    c: Coincident(g2,g1)
    c: Coincident(g1,g7)
    c: Vertical(g1)
    c: PointOnObject(g0,g-1)
    c: DistanceX(g7) = 4
    c: Coincident(g4,g2)
    c: Horizontal(g2)
    c: Coincident(g3,g4)
    c: Horizontal(g3)
    c: Coincident(g5,g6)
    c: Horizontal(g5)
    c: Coincident(g6,g7)
    c: Horizontal(g7)
    c: Radius(g0) = 1.5
    c: Vertical(g5,g3)
    c: DistanceX(g6,g6) = 3
    c: Equal(g4,g6)
    c: Equal(g3,g5)
    c: Vertical(g0,g0)
    c: DistanceX(g2) = -4
    c: Vertical(g2,g6)
FEATURE [Sketcher::SketchObject] Sketch
  ArcFitTolerance = 1e-06
  AttachmentOffset = pos=(0,0,0) rot=(0,0,1;-1.5708rad)
  AttachmentSupport = -> [YZ_Plane003]
  FullyConstrained = false
  MakeInternals = false
  MapMode = 5
  Placement = pos=(0,0,0) rot=(0,-1,0;4.71239rad)
  sketch-geometry (18):
    g0-g3: Circle [constr] x4 (B-spline internal-alignment scaffolding for g4; pole/knot coordinates omitted)
    g4: BSplineCurve PolesCount=6 KnotsCount=3 Degree=3 IsPeriodic=0
    g5: GeomPoint [constr] X=1.75 Y=-5 Z=0
    g6: GeomPoint [constr] X=0 Y=-4 Z=0
    g7: GeomPoint [constr] X=-1.75 Y=-5 Z=0
    g8: Circle [constr] CenterX=0.442329 CenterY=-4 CenterZ=0 NormalX=0 NormalY=0 NormalZ=1 AngleXU=0 Radius=1
    g9: Circle [constr] CenterX=-0.442329 CenterY=-4 CenterZ=0 NormalX=0 NormalY=0 NormalZ=1 AngleXU=0 Radius=1
    g10: LineSegment [constr] StartX=-1.75 StartY=-5 StartZ=0 EndX=-1.30767 EndY=-5 EndZ=0
    g11: LineSegment [constr] StartX=1.30767 StartY=-5 StartZ=0 EndX=1.75 EndY=-5 EndZ=0
    g12: LineSegment [constr] StartX=0.442329 StartY=-4 StartZ=0 EndX=1.30767 EndY=-5 EndZ=0
    g13: LineSegment [constr] StartX=-0.442329 StartY=-4 StartZ=0 EndX=0 EndY=-4 EndZ=0
    g14: LineSegment [constr] StartX=0.442329 StartY=-4 StartZ=0 EndX=0 EndY=-4 EndZ=0
    g15: LineSegment StartX=-1.75 StartY=-5 StartZ=0 EndX=-1.75 EndY=-7.07699 EndZ=0
    g16: LineSegment StartX=-1.75 StartY=-7.07699 StartZ=0 EndX=1.75 EndY=-7.07699 EndZ=0
    g17: LineSegment StartX=1.75 StartY=-7.07699 StartZ=0 EndX=1.75 EndY=-5 EndZ=0
  constraints (40):
    c: Weight(g0) = 1
    c: Equal(g0,g1)
    c: Equal(g0,g2)
    c: Equal(g0,g3)
    c: InternalAlignment(g0-g3 -> g4) x4
    c: InternalAlignment(g5,g4)
    c: InternalAlignment(g6,g4)
    c: InternalAlignment(g7,g4)
    c: Horizontal(g2,g4)
    c: Horizontal(g4,g1)
    c: Horizontal(g1,g4)
    c: PointOnObject(g6,g-2)
    c: DistanceY(g4) = -5
    c: InternalAlignment(g8,g4)
    c: Equal(g8,g0)
    c: InternalAlignment(g9,g4)
    c: Equal(g9,g0)
    c: Horizontal(g8,g9)
    c: Coincident(g10,g4)
    c: Coincident(g10,g2)
    c: Coincident(g11,g1)
    c: Coincident(g11,g4)
    c: Coincident(g12,g8)
    c: Coincident(g12,g1)
    c: Coincident(g13,g9)
    c: Coincident(g13,g6)
    c: Coincident(g14,g8)
    c: Coincident(g14,g6)
    c: Equal(g14,g11)
    c: Equal(g13,g10)
    c: DistanceX(g4) = 1.75
    c: DistanceX(g4) = -1.75
    c: DistanceY(g6) = -4
    c: Coincident(g15,g4)
    c: Vertical(g15)
    c: Coincident(g15,g16)
    c: Horizontal(g16)
    c: Coincident(g16,g17)
    c: Coincident(g17,g4)
    c: Vertical(g17)
FEATURE [PartDesign::Pocket] Pocket004
  BaseFeature = -> Pocket002
  Direction = (-1,0,0)
  Length = 5
  Length2 = 5
  Placement = pos=(0,0,0) rot=(1,0,0;1.5708rad)
  Profile = -> Sketch
  ReferenceAxis = -> Sketch [N_Axis]
  Refine = true
  Reversed = true
  Suppressed = false
  Type = 0
FEATURE [PartDesign::PolarPattern] PolarPattern001
  Angle = 360
  Axis = -> Y_Axis003
  BaseFeature = -> Pocket002
  Mode = 1
  Occurrences = 4
  Offset = 120
  Originals = -> [Pocket004]
  Placement = pos=(0,0,0) rot=(1,0,0;1.5708rad)
  Refine = true
  Suppressed = false
  TransformMode = 0
FEATURE [PartDesign::Pocket] Pocket005
  BaseFeature = -> PolarPattern001
  Direction = (0,0,-1)
  Length = 5
  Length2 = 5
  Midplane = true
  Placement = pos=(0,0,0) rot=(1,0,0;1.5708rad)
  Profile = -> Sketch016
  ReferenceAxis = -> Sketch016 [N_Axis]
  Refine = true
  Suppressed = false
  Type = 1
FEATURE [PartDesign::Body] Body003  label="B001"
  AllowCompound = false
  Group = -> [Sketch008,Pad005,Sketch009,Pocket002,Pocket004,Sketch016,PolarPattern001,Sketch,Pocket005]
  Origin = -> Origin003
  Tip = -> Pocket005
FEATURE [PartDesign::FeatureBase] Clone
  BaseFeature = -> Body003
  Suppressed = false
FEATURE [PartDesign::Body] Body005
  AllowCompound = false
  Group = -> [Clone]
  Origin = -> Origin005
  Placement = pos=(0,0,0) rot=(0,1,0;4.18879rad)
  Tip = -> Clone
FEATURE [Part::Cut] Cut
  Base = -> Box
  Refine = true
  Tool = -> Body003
FEATURE [Part::Mirroring] Part__Mirroring001  label="B001 (Mirror #2)"
  Base = (0,0,0)
  Normal = (0,1,0)
  Source = -> Body003
FEATURE [Part::MultiFuse] Fusion001
  Refine = true
  Shapes = -> [Body003,Part__Mirroring001]
FEATURE [PartDesign::SubShapeBinder] Binder
  BindCopyOnChange = 0
  BindMode = 0
  ClaimChildren = false
  Context = -> Body004 [Binder.]
  Fuse = false
  MakeFace = true
  OffsetFill = false
  OffsetIntersection = false
  OffsetJoinType = 0
  OffsetOpenResult = false
  PartialLoad = false
  Placement = pos=(0,-0.2,0) rot=(0,0,1;0rad)
  Refine = true
  Relative = true
  Support = -> [Body003[Sketch.]]
  _Version = 2
FEATURE [PartDesign::Pad] Pad
  BaseFeature = -> Pad006
  Direction = (1,0,0)
  Length = 6
  Length2 = 10
  Placement = pos=(0,0,0) rot=(1,0,0;1.5708rad)
  Profile = -> Binder
  Refine = true
  Suppressed = false
  Type = 0
FEATURE [PartDesign::PolarPattern] PolarPattern002
  Angle = 360
  Axis = -> Y_Axis004
  BaseFeature = -> Pad
  Mode = 0
  Occurrences = 3
  Offset = 120
  Originals = -> [Pad]
  Placement = pos=(0,0,0) rot=(1,0,0;1.5708rad)
  Refine = true
  Suppressed = false
  TransformMode = 0
FEATURE [PartDesign::Pad] Pad008
  BaseFeature = -> PolarPattern002
  Direction = (0,-1,2e-16)
  Length = 4.8
  Length2 = 10
  Placement = pos=(0,0,0) rot=(1,0,0;1.5708rad)
  Profile = -> Sketch012
  ReferenceAxis = -> Sketch012 [N_Axis]
  Refine = true
  Suppressed = false
  Type = 0
FEATURE [Sketcher::SketchObject] Sketch017
  ArcFitTolerance = 1e-06
  AttachmentSupport = -> [XZ_Plane004]
  FullyConstrained = false
  MakeInternals = false
  MapMode = 5
  Placement = pos=(0,0,0) rot=(1,0,0;1.5708rad)
  sketch-geometry (8):
    g0: LineSegment StartX=-27 StartY=3.5 StartZ=0 EndX=-27 EndY=-2.5 EndZ=0
    g1: LineSegment StartX=-27 StartY=-2.5 StartZ=0 EndX=8 EndY=-2.5 EndZ=0
    g2: LineSegment StartX=8 StartY=-2.5 StartZ=0 EndX=8 EndY=3.5 EndZ=0
    g3: LineSegment StartX=8 StartY=3.5 StartZ=0 EndX=-27 EndY=3.5 EndZ=0
    g4: LineSegment StartX=-82.4426 StartY=43.1102 StartZ=0 EndX=-82.4426 EndY=-32.4768 EndZ=0
    g5: LineSegment StartX=-82.4426 StartY=-32.4768 StartZ=0 EndX=65.6399 EndY=-32.4768 EndZ=0
    g6: LineSegment StartX=65.6399 StartY=-32.4768 StartZ=0 EndX=65.6399 EndY=43.1102 EndZ=0
    g7: LineSegment StartX=65.6399 StartY=43.1102 StartZ=0 EndX=-82.4426 EndY=43.1102 EndZ=0
  constraints (20):
    c: Coincident(g0,g1)
    c: Coincident(g1,g2)
    c: Coincident(g2,g3)
    c: Coincident(g3,g0)
    c: Vertical(g2)
    c: Horizontal(g1)
    c: Horizontal(g3)
    c: Distance(g0,g2) = 35
    c: Distance(g1,g3) = 6
    c: DistanceY(g0) = -2.5
    c: DistanceX(g2) = 8
    c: Vertical(g0)
    c: Coincident(g4,g5)
    c: Coincident(g5,g6)
    c: Coincident(g6,g7)
    c: Coincident(g7,g4)
    c: Vertical(g4)
    c: Vertical(g6)
    c: Horizontal(g5)
    c: Horizontal(g7)
FEATURE [PartDesign::Pocket] Pocket
  BaseFeature = -> Pad008
  Direction = (0,1,-2e-16)
  Length = 5
  Length2 = 5
  Midplane = true
  Placement = pos=(0,0,0) rot=(1,0,0;1.5708rad)
  Profile = -> Sketch017
  ReferenceAxis = -> Sketch017 [N_Axis]
  Refine = true
  Suppressed = false
  Type = 1
FEATURE [Sketcher::SketchObject] Sketch018
  ArcFitTolerance = 1e-06
  AttachmentSupport = -> [Pocket]
  FullyConstrained = true
  MakeInternals = false
  MapMode = 5
  Placement = pos=(0,-1.1e-15,-2.5) rot=(1,0,0;3.14159rad)
  sketch-geometry (5):
    g0: LineSegment StartX=-26 StartY=-5 StartZ=0 EndX=-26 EndY=5.2 EndZ=0
    g1: LineSegment StartX=-26 StartY=5.2 StartZ=0 EndX=-19.4182 EndY=9 EndZ=0
    g2: LineSegment StartX=-19.4182 StartY=9 StartZ=0 EndX=-17.2243 EndY=5.2 EndZ=0
    g3: LineSegment StartX=-17.2243 StartY=5.2 StartZ=0 EndX=-17.2243 EndY=-5 EndZ=0
    g4: LineSegment StartX=-17.2243 StartY=-5 StartZ=0 EndX=-26 EndY=-5 EndZ=0
  constraints (15):
    c: Coincident(g1,g2)
    c: Coincident(g2,g3)
    c: Vertical(g3)
    c: Coincident(g3,g4)
    c: Horizontal(g4)
    c: Angle(g0,g1) = 2.0944
    c: Perpendicular(g1,g2)
    c: DistanceY(g1) = 9
    c: Equal(g3,g0)
    c: Coincident(g1,g0)
    c: Vertical(g0)
    c: Coincident(g0,g4)
    c: DistanceX(g0) = -26
    c: DistanceY(g0) = 5.2
    c: DistanceY(g0) = -5
FEATURE [PartDesign::Pocket] Pocket006
  BaseFeature = -> Pocket
  Direction = (0,0,1)
  Length = 2.5
  Length2 = 5
  Placement = pos=(0,0,0) rot=(1,0,0;1.5708rad)
  Profile = -> Sketch018
  ReferenceAxis = -> Sketch018 [N_Axis]
  Refine = true
  Suppressed = false
  TaperAngle = -30
  Type = 0
FEATURE [PartDesign::Body] Body004  label="B002"
  AllowCompound = true
  Group = -> [Sketch010,Pad006,Sketch012,Binder,Pad,PolarPattern002,Sketch017,Pad008,Pocket,Sketch018,Pocket006]
  Origin = -> Origin004
  Tip = -> Pocket006
FEATURE [Part::Cut] Cut001
  Base = -> Cut
  Refine = true
  Tool = -> Body004
FEATURE [Part::Mirroring] Part__Mirroring  label="Cut001 (Mirror #1)"
  Base = (-26,-2e-16,-2.5)
  MirrorPlane = -> Cut001 [Face1]
  Normal = (0,1,0)
  Source = -> Cut001
FEATURE [Part::MultiFuse] Fusion
  Refine = true
  Shapes = -> [Cut001,Part__Mirroring]
FEATURE [Part::Mirroring] Part__Mirroring002  label="B002 (Mirror #3)"
  Base = (0,0,0)
  Normal = (0,1,0)
  Source = -> Body004
FEATURE [Part::MultiFuse] Fusion002
  Refine = true
  Shapes = -> [Body004,Part__Mirroring002]
FEATURE [Part::Compound] Compound
  Links = -> [Fusion001,Fusion002]
FEATURE [Mesh::Feature] Mesh  label="Compound (Meshed)"
PROVENANCE & LICENSES
A FreeCAD (.FCStd) document from a public repository crawl; recipes are the document's own serialized feature recipes (and, for linked parts, companion documents' recipes).
License: as declared in the source repository (recorded in the dataset sidecar).
